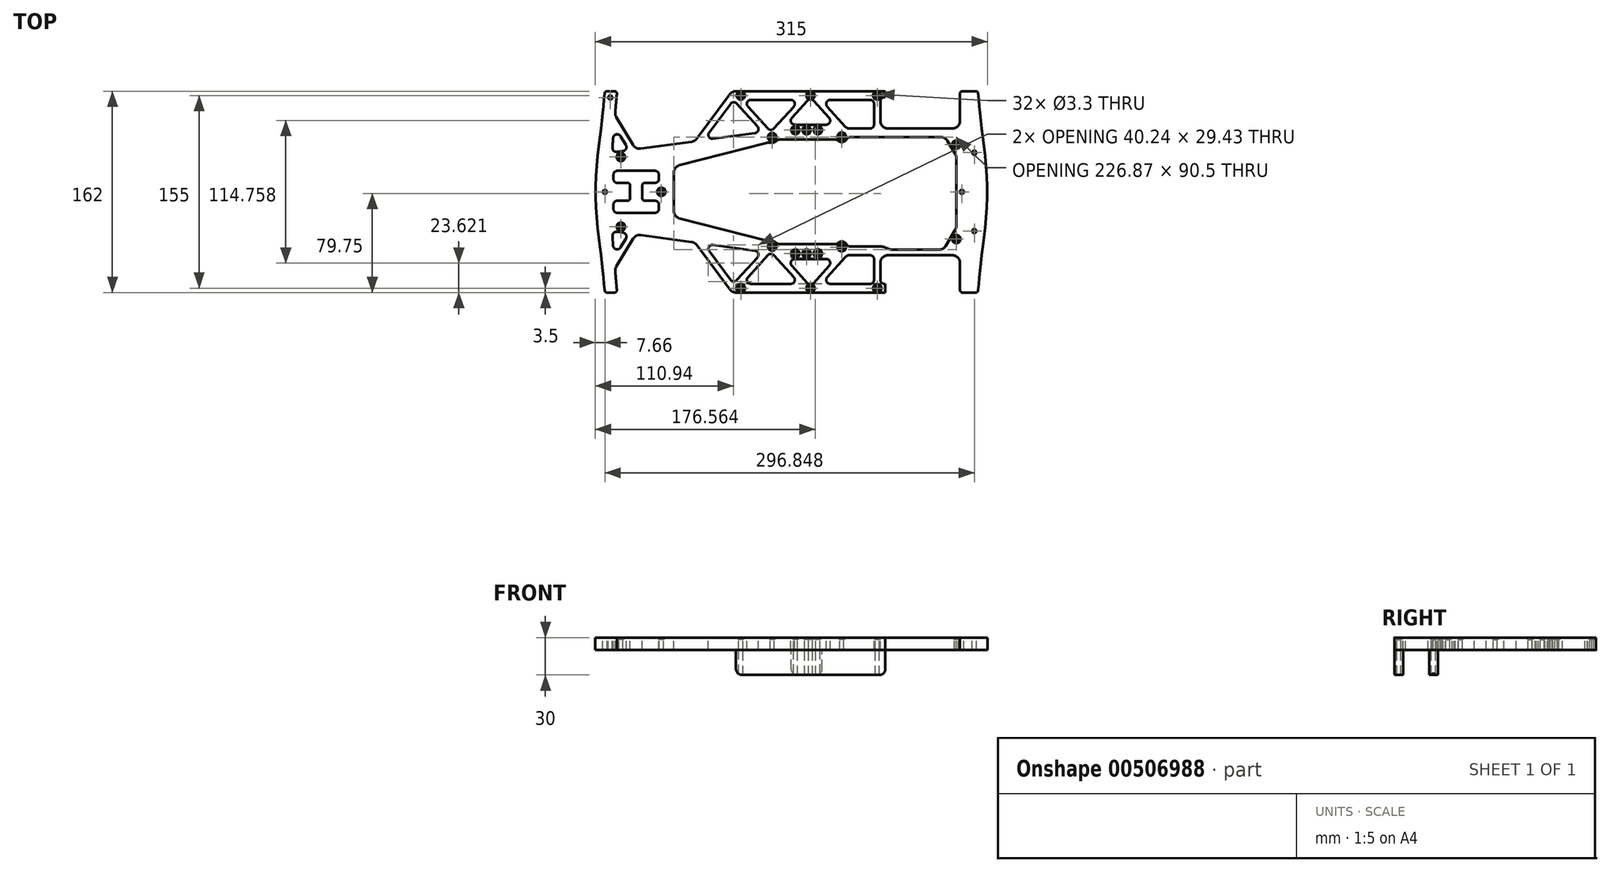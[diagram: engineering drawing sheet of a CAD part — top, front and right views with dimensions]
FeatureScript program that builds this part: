
annotation { "Feature Type Name" : "Feature", "Feature Type Description" : "" }
export const myFeature = defineFeature(function(context is Context, id is Id, definition is map)
    precondition{}
    {
        {
            var Q0;
            Q0=qCreatedBy(makeId("Top.planeOp"),FACE);
            var sketch = newSketch(context, id + "F0", { "sketchPlane" : qUnion([Q0])});
            skLineSegment(sketch, "E0", {"start": v(-44.5, 81) * mm, "end": v(75.5, 81) * mm});
            skLineSegment(sketch, "E1", {"start": v(30.36, 59.43) * mm, "end": v(17.78, 73.34) * mm});
            skLineSegment(sketch, "E2", {"start": v(0.38, 59.43) * mm, "end": v(12.96, 73.34) * mm});
            skLineSegment(sketch, "E3", {"start": v(14.9, 74) * mm, "end": v(15.85, 74) * mm});
            skLineSegment(sketch, "E4", {"start": v(31.25, 74) * mm, "end": v(63.25, 74) * mm});
            skLineSegment(sketch, "E5", {"start": v(-32.5, 74) * mm, "end": v(-0.5, 74) * mm});
            skLineSegment(sketch, "E6", {"start": v(74.75, -74) * mm, "end": v(75.5, -74) * mm});
            skLineSegment(sketch, "E7", {"start": v(31.25, -74) * mm, "end": v(63.25, -74) * mm});
            skLineSegment(sketch, "E8", {"start": v(-32.5, -74) * mm, "end": v(-0.5, -74) * mm});
            skArc(sketch, "E9", {"start": v(131.64, -30.72) * mm, "mid": v(132.28, -29.23) * mm, "end": v(132.5, -27.62) * mm});
            skArc(sketch, "E10", {"start": v(118.73, -46.5) * mm, "mid": v(121.68, -45.72) * mm, "end": v(123.87, -43.6) * mm});
            skArc(sketch, "E11", {"start": v(132.5, 27.62) * mm, "mid": v(132.28, 29.23) * mm, "end": v(131.64, 30.72) * mm});
            skArc(sketch, "E12", {"start": v(125.37, 41.1) * mm, "mid": v(123.19, 43.22) * mm, "end": v(120.24, 44) * mm});
            skLineSegment(sketch, "E13", {"start": v(131.64, 30.72) * mm, "end": v(125.37, 41.1) * mm});
            skArc(sketch, "E14", {"start": v(-89.87, 21.37) * mm, "mid": v(-93.11, 19.23) * mm, "end": v(-94.37, 15.56) * mm});
            skArc(sketch, "E15", {"start": v(-94.37, -15.56) * mm, "mid": v(-93.11, -19.23) * mm, "end": v(-89.87, -21.37) * mm});
            skLineSegment(sketch, "E16", {"start": v(-94.37, -15.56) * mm, "end": v(-94.37, 15.56) * mm});
            skLineSegment(sketch, "E17", {"start": v(131.64, -30.72) * mm, "end": v(123.87, -43.6) * mm});
            skLineSegment(sketch, "E18", {"start": v(-139.75, 16.9) * mm, "end": v(-109.62, 16.9) * mm});
            skLineSegment(sketch, "E19", {"start": v(-139.75, 7.13) * mm, "end": v(-129.57, 7.13) * mm});
            skLineSegment(sketch, "E20", {"start": v(-129.57, -7.13) * mm, "end": v(-129.57, 7.13) * mm});
            skLineSegment(sketch, "E21", {"start": v(-139.75, -7.13) * mm, "end": v(-129.57, -7.13) * mm});
            skLineSegment(sketch, "E22", {"start": v(-139.75, -16.9) * mm, "end": v(-109.62, -16.9) * mm});
            skLineSegment(sketch, "E23", {"start": v(-143, -13.64) * mm, "end": v(-143, -10.38) * mm});
            skLineSegment(sketch, "E24", {"start": v(-143, 10.38) * mm, "end": v(-143, 13.64) * mm});
            skLineSegment(sketch, "E25", {"start": v(-106.37, 13.64) * mm, "end": v(-106.37, 10.38) * mm});
            skLineSegment(sketch, "E26", {"start": v(-106.37, -10.38) * mm, "end": v(-106.37, -13.64) * mm});
            skLineSegment(sketch, "E27", {"start": v(-119.8, -7.13) * mm, "end": v(-109.62, -7.13) * mm});
            skLineSegment(sketch, "E28", {"start": v(-119.8, 7.13) * mm, "end": v(-109.62, 7.13) * mm});
            skLineSegment(sketch, "E29", {"start": v(-119.8, -7.13) * mm, "end": v(-119.8, 7.13) * mm});
            skArc(sketch, "E30", {"start": v(-12.16, -40.95) * mm, "mid": v(-13.66, -39.88) * mm, "end": v(-15.47, -39.5) * mm});
            skArc(sketch, "E31", {"start": v(-15.47, 39.5) * mm, "mid": v(-13.66, 39.88) * mm, "end": v(-12.16, 40.95) * mm});
            skLineSegment(sketch, "E32", {"start": v(2.79, -54) * mm, "end": v(27.95, -54) * mm});
            skLineSegment(sketch, "E33", {"start": v(0.38, -59.43) * mm, "end": v(12.96, -73.34) * mm});
            skLineSegment(sketch, "E34", {"start": v(30.36, -59.43) * mm, "end": v(17.78, -73.34) * mm});
            skLineSegment(sketch, "E35", {"start": v(2.79, 54) * mm, "end": v(27.95, 54) * mm});
            skLineSegment(sketch, "E36", {"start": v(-121.14, 34.71) * mm, "end": v(-80.12, 40.32) * mm});
            skLineSegment(sketch, "E37", {"start": v(-76.13, 42.67) * mm, "end": v(-49.3, 78.59) * mm});
            skArc(sketch, "E38", {"start": v(-18.67, 39.5) * mm, "mid": v(-19.42, 39.45) * mm, "end": v(-20.17, 39.31) * mm});
            skArc(sketch, "E39", {"start": v(79.02, -46.15) * mm, "mid": v(80.02, -46.41) * mm, "end": v(81.04, -46.5) * mm});
            skArc(sketch, "E40", {"start": v(73.98, -44.35) * mm, "mid": v(72.98, -44.09) * mm, "end": v(71.96, -44) * mm});
            skLineSegment(sketch, "E41", {"start": v(81.04, -46.5) * mm, "end": v(82.68, -46.5) * mm});
            skLineSegment(sketch, "E42", {"start": v(73.98, -44.35) * mm, "end": v(79.02, -46.15) * mm});
            skLineSegment(sketch, "E43", {"start": v(81.04, -46.5) * mm, "end": v(118.73, -46.5) * mm});
            skLineSegment(sketch, "E44", {"start": v(77.5, 51) * mm, "end": v(129.5, 51) * mm});
            skArc(sketch, "E45", {"start": v(135.5, -57) * mm, "mid": v(133.74, -52.76) * mm, "end": v(129.5, -51) * mm});
            skLineSegment(sketch, "E46", {"start": v(135.5, -81) * mm, "end": v(135.5, -57) * mm});
            skArc(sketch, "E47", {"start": v(129.5, 51) * mm, "mid": v(133.74, 52.76) * mm, "end": v(135.5, 57) * mm});
            skLineSegment(sketch, "E48", {"start": v(135.5, 81) * mm, "end": v(135.5, 57) * mm});
            skLineSegment(sketch, "E49", {"start": v(132.5, 0) * mm, "end": v(132.5, 27.62) * mm});
            skLineSegment(sketch, "E50", {"start": v(150, 81) * mm, "end": v(135.5, 81) * mm});
            skArc(sketch, "E51", {"start": v(37.48, 41.16) * mm, "mid": v(41.24, 40.06) * mm, "end": v(44.44, 42.32) * mm});
            skLineSegment(sketch, "E52", {"start": v(47.28, 44) * mm, "end": v(120.24, 44) * mm});
            skLineSegment(sketch, "E53", {"start": v(46.18, 51) * mm, "end": v(63.25, 51) * mm});
            skArc(sketch, "E54", {"start": v(71.5, 57) * mm, "mid": v(73.26, 52.76) * mm, "end": v(77.5, 51) * mm});
            skLineSegment(sketch, "E55", {"start": v(71.5, 57) * mm, "end": v(71.5, 72.75) * mm});
            skLineSegment(sketch, "E56", {"start": v(66.5, 54.25) * mm, "end": v(66.5, 70.75) * mm});
            skLineSegment(sketch, "E57", {"start": v(75.5, 76) * mm, "end": v(75.5, 81) * mm});
            skLineSegment(sketch, "E58", {"start": v(74.75, 76) * mm, "end": v(75.5, 76) * mm});
            skLineSegment(sketch, "E59", {"start": v(43.77, 52.07) * mm, "end": v(28.84, 68.57) * mm});
            skLineSegment(sketch, "E60", {"start": v(-9.77, 42) * mm, "end": v(35.3, 42) * mm});
            skLineSegment(sketch, "E61", {"start": v(-18.67, 39.5) * mm, "end": v(-15.47, 39.5) * mm});
            skLineSegment(sketch, "E62", {"start": v(-63, 42.66) * mm, "end": v(-29.24, 47.28) * mm});
            skLineSegment(sketch, "E63", {"start": v(-27.27, 52.68) * mm, "end": v(-43.87, 71.03) * mm});
            skLineSegment(sketch, "E64", {"start": v(-18.9, 50.89) * mm, "end": v(-34.9, 68.57) * mm});
            skLineSegment(sketch, "E65", {"start": v(-14.1, 50.89) * mm, "end": v(1.9, 68.57) * mm});
            skArc(sketch, "E66", {"start": v(-44.5, 81) * mm, "mid": v(-47.19, 80.36) * mm, "end": v(-49.3, 78.59) * mm});
            skArc(sketch, "E67", {"start": v(-80.12, 40.32) * mm, "mid": v(-77.89, 41.1) * mm, "end": v(-76.13, 42.67) * mm});
            skLineSegment(sketch, "E68", {"start": v(-66.04, 47.83) * mm, "end": v(-48.89, 70.8) * mm});
            skLineSegment(sketch, "E69", {"start": v(-20.17, 39.31) * mm, "end": v(-89.87, 21.37) * mm});
            skArc(sketch, "E70", {"start": v(-127.1, 37.56) * mm, "mid": v(-124.54, 35.24) * mm, "end": v(-121.14, 34.71) * mm});
            skLineSegment(sketch, "E71", {"start": v(-140.08, 32.12) * mm, "end": v(-135.33, 32.77) * mm});
            skLineSegment(sketch, "E72", {"start": v(-132.99, 37.66) * mm, "end": v(-137.22, 44.7) * mm});
            skFitSpline(sketch, "E73", {"points": [v(-143.24, 43.25) * mm, v(-143.43, 40.68) * mm, v(-143.6, 38.12) * mm, v(-143.77, 35.55) * mm]});
            skLineSegment(sketch, "E74", {"start": v(-150, 81) * mm, "end": v(-140, 81) * mm});
            skFitSpline(sketch, "E75", {"points": [v(-140, 81) * mm, v(-140.53, 75.29) * mm, v(-141.06, 69.57) * mm, v(-141.56, 63.86) * mm]});
            skLineSegment(sketch, "E76", {"start": v(-127.1, 37.56) * mm, "end": v(-140.73, 60.24) * mm});
            skArc(sketch, "E77", {"start": v(-141.56, 63.86) * mm, "mid": v(-141.43, 61.98) * mm, "end": v(-140.73, 60.24) * mm});
            skLineSegment(sketch, "E78", {"start": v(43.77, -52.07) * mm, "end": v(28.84, -68.57) * mm});
            skArc(sketch, "E79", {"start": v(77.5, -51) * mm, "mid": v(73.26, -52.76) * mm, "end": v(71.5, -57) * mm});
            skLineSegment(sketch, "E80", {"start": v(47.28, -44) * mm, "end": v(71.96, -44) * mm});
            skArc(sketch, "E81", {"start": v(-140.73, -60.24) * mm, "mid": v(-141.43, -61.98) * mm, "end": v(-141.56, -63.86) * mm});
            skArc(sketch, "E82", {"start": v(-121.14, -34.71) * mm, "mid": v(-124.54, -35.24) * mm, "end": v(-127.1, -37.56) * mm});
            skArc(sketch, "E83", {"start": v(-76.13, -42.67) * mm, "mid": v(-77.89, -41.1) * mm, "end": v(-80.12, -40.32) * mm});
            skArc(sketch, "E84", {"start": v(-49.3, -78.59) * mm, "mid": v(-47.19, -80.36) * mm, "end": v(-44.5, -81) * mm});
            skArc(sketch, "E85", {"start": v(-20.17, -39.31) * mm, "mid": v(-19.42, -39.45) * mm, "end": v(-18.67, -39.5) * mm});
            skFitSpline(sketch, "E86", {"points": [v(-143.24, -43.25) * mm, v(-143.43, -40.68) * mm, v(-143.6, -38.12) * mm, v(-143.77, -35.55) * mm]});
            skLineSegment(sketch, "E87", {"start": v(-121.14, -34.71) * mm, "end": v(-80.12, -40.32) * mm});
            skLineSegment(sketch, "E88", {"start": v(-140.08, -32.12) * mm, "end": v(-135.33, -32.77) * mm});
            skLineSegment(sketch, "E89", {"start": v(-127.1, -37.56) * mm, "end": v(-140.73, -60.24) * mm});
            skLineSegment(sketch, "E90", {"start": v(-132.99, -37.66) * mm, "end": v(-137.22, -44.7) * mm});
            skLineSegment(sketch, "E91", {"start": v(-63, -42.66) * mm, "end": v(-29.24, -47.28) * mm});
            skLineSegment(sketch, "E92", {"start": v(77.5, -51) * mm, "end": v(129.5, -51) * mm});
            skLineSegment(sketch, "E93", {"start": v(-150, -81) * mm, "end": v(-140, -81) * mm});
            skLineSegment(sketch, "E94", {"start": v(-14.1, -50.89) * mm, "end": v(1.9, -68.57) * mm});
            skLineSegment(sketch, "E95", {"start": v(-18.9, -50.89) * mm, "end": v(-34.9, -68.57) * mm});
            skLineSegment(sketch, "E96", {"start": v(-27.27, -52.68) * mm, "end": v(-43.87, -71.03) * mm});
            skLineSegment(sketch, "E97", {"start": v(132.5, 0) * mm, "end": v(132.5, -27.62) * mm});
            skFitSpline(sketch, "E98", {"points": [v(-150, -81) * mm, v(-152.5, -54) * mm, v(-157.5, 0) * mm, v(-152.5, 54) * mm, v(-150, 81) * mm]});
            skFitSpline(sketch, "E99", {"points": [v(150, 81) * mm, v(152.5, 54) * mm, v(157.5, 0) * mm, v(152.5, -54) * mm, v(150, -81) * mm]});
            skLineSegment(sketch, "E100", {"start": v(-76.13, -42.67) * mm, "end": v(-49.3, -78.59) * mm});
            skLineSegment(sketch, "E101", {"start": v(75.5, -74) * mm, "end": v(75.5, -81) * mm});
            skLineSegment(sketch, "E102", {"start": v(150, -81) * mm, "end": v(135.5, -81) * mm});
            skLineSegment(sketch, "E103", {"start": v(-44.5, -81) * mm, "end": v(75.5, -81) * mm});
            skLineSegment(sketch, "E104", {"start": v(-66.04, -47.83) * mm, "end": v(-48.89, -70.8) * mm});
            skFitSpline(sketch, "E105", {"points": [v(-140, -81) * mm, v(-140.53, -75.29) * mm, v(-141.06, -69.57) * mm, v(-141.56, -63.86) * mm]});
            skLineSegment(sketch, "E106", {"start": v(66.5, -54.25) * mm, "end": v(66.5, -70.75) * mm});
            skLineSegment(sketch, "E107", {"start": v(71.5, -57) * mm, "end": v(71.5, -70.75) * mm});
            skLineSegment(sketch, "E108", {"start": v(46.18, -51) * mm, "end": v(63.25, -51) * mm});
            skArc(sketch, "E109", {"start": v(44.44, -42.32) * mm, "mid": v(41.24, -40.06) * mm, "end": v(37.48, -41.16) * mm});
            skLineSegment(sketch, "E110", {"start": v(-18.67, -39.5) * mm, "end": v(-15.47, -39.5) * mm});
            skLineSegment(sketch, "E111", {"start": v(-9.77, -42) * mm, "end": v(35.3, -42) * mm});
            skLineSegment(sketch, "E112", {"start": v(-20.17, -39.31) * mm, "end": v(-89.87, -21.37) * mm});
            skArc(sketch, "E113", {"start": v(-137.22, 44.7) * mm, "mid": v(-140.76, 46.18) * mm, "end": v(-143.24, 43.25) * mm});
            skArc(sketch, "E114", {"start": v(-135.33, 32.77) * mm, "mid": v(-132.84, 34.59) * mm, "end": v(-132.99, 37.66) * mm});
            skArc(sketch, "E115", {"start": v(-143.77, 35.55) * mm, "mid": v(-142.74, 32.96) * mm, "end": v(-140.08, 32.12) * mm});
            skArc(sketch, "E116", {"start": v(-139.75, 16.9) * mm, "mid": v(-142.05, 15.94) * mm, "end": v(-143, 13.64) * mm});
            skArc(sketch, "E117", {"start": v(-143, 10.38) * mm, "mid": v(-142.05, 8.08) * mm, "end": v(-139.75, 7.13) * mm});
            skArc(sketch, "E118", {"start": v(-106.37, 13.64) * mm, "mid": v(-107.32, 15.94) * mm, "end": v(-109.62, 16.9) * mm});
            skArc(sketch, "E119", {"start": v(-109.62, 7.13) * mm, "mid": v(-107.32, 8.08) * mm, "end": v(-106.37, 10.38) * mm});
            skArc(sketch, "E120", {"start": v(-106.37, -10.38) * mm, "mid": v(-107.32, -8.08) * mm, "end": v(-109.62, -7.13) * mm});
            skArc(sketch, "E121", {"start": v(-109.62, -16.9) * mm, "mid": v(-107.32, -15.94) * mm, "end": v(-106.37, -13.64) * mm});
            skArc(sketch, "E122", {"start": v(-139.75, -7.13) * mm, "mid": v(-142.05, -8.08) * mm, "end": v(-143, -10.38) * mm});
            skArc(sketch, "E123", {"start": v(-143, -13.64) * mm, "mid": v(-142.05, -15.94) * mm, "end": v(-139.75, -16.9) * mm});
            skArc(sketch, "E124", {"start": v(-140.08, -32.12) * mm, "mid": v(-142.74, -32.96) * mm, "end": v(-143.77, -35.55) * mm});
            skArc(sketch, "E125", {"start": v(-143.24, -43.25) * mm, "mid": v(-140.76, -46.18) * mm, "end": v(-137.22, -44.7) * mm});
            skArc(sketch, "E126", {"start": v(-132.99, -37.66) * mm, "mid": v(-132.84, -34.59) * mm, "end": v(-135.33, -32.77) * mm});
            skArc(sketch, "E127", {"start": v(-63, -42.66) * mm, "mid": v(-66.23, -44.23) * mm, "end": v(-66.04, -47.83) * mm});
            skArc(sketch, "E128", {"start": v(-27.27, -52.68) * mm, "mid": v(-26.63, -49.38) * mm, "end": v(-29.24, -47.28) * mm});
            skArc(sketch, "E129", {"start": v(-48.89, -70.8) * mm, "mid": v(-46.44, -72.1) * mm, "end": v(-43.87, -71.03) * mm});
            skArc(sketch, "E130", {"start": v(-14.1, -50.89) * mm, "mid": v(-16.5, -49.82) * mm, "end": v(-18.9, -50.89) * mm});
            skArc(sketch, "E131", {"start": v(-34.9, -68.57) * mm, "mid": v(-35.47, -72.07) * mm, "end": v(-32.5, -74) * mm});
            skArc(sketch, "E132", {"start": v(-0.5, -74) * mm, "mid": v(2.47, -72.07) * mm, "end": v(1.9, -68.57) * mm});
            skArc(sketch, "E133", {"start": v(2.79, -54) * mm, "mid": v(-0.18, -55.93) * mm, "end": v(0.38, -59.43) * mm});
            skArc(sketch, "E134", {"start": v(12.96, -73.34) * mm, "mid": v(15.37, -74.4) * mm, "end": v(17.78, -73.34) * mm});
            skArc(sketch, "E135", {"start": v(30.36, -59.43) * mm, "mid": v(30.92, -55.93) * mm, "end": v(27.95, -54) * mm});
            skArc(sketch, "E136", {"start": v(28.84, -68.57) * mm, "mid": v(28.28, -72.07) * mm, "end": v(31.25, -74) * mm});
            skArc(sketch, "E137", {"start": v(46.18, -51) * mm, "mid": v(44.86, -51.28) * mm, "end": v(43.77, -52.07) * mm});
            skArc(sketch, "E138", {"start": v(66.5, -54.25) * mm, "mid": v(65.55, -51.95) * mm, "end": v(63.25, -51) * mm});
            skArc(sketch, "E139", {"start": v(63.25, -74) * mm, "mid": v(65.55, -73.05) * mm, "end": v(66.5, -70.75) * mm});
            skArc(sketch, "E140", {"start": v(71.5, -70.75) * mm, "mid": v(72.45, -73.05) * mm, "end": v(74.75, -74) * mm});
            skArc(sketch, "E141", {"start": v(-12.16, -40.95) * mm, "mid": v(-11.07, -41.73) * mm, "end": v(-9.77, -42) * mm});
            skArc(sketch, "E142", {"start": v(35.3, -42) * mm, "mid": v(36.47, -41.78) * mm, "end": v(37.48, -41.16) * mm});
            skArc(sketch, "E143", {"start": v(44.44, -42.32) * mm, "mid": v(45.63, -43.55) * mm, "end": v(47.28, -44) * mm});
            skArc(sketch, "E144", {"start": v(-9.77, 42) * mm, "mid": v(-11.07, 41.73) * mm, "end": v(-12.16, 40.95) * mm});
            skArc(sketch, "E145", {"start": v(37.48, 41.16) * mm, "mid": v(36.47, 41.78) * mm, "end": v(35.3, 42) * mm});
            skArc(sketch, "E146", {"start": v(47.28, 44) * mm, "mid": v(45.63, 43.55) * mm, "end": v(44.44, 42.32) * mm});
            skArc(sketch, "E147", {"start": v(-66.04, 47.83) * mm, "mid": v(-66.23, 44.23) * mm, "end": v(-63, 42.66) * mm});
            skArc(sketch, "E148", {"start": v(-43.87, 71.03) * mm, "mid": v(-46.44, 72.1) * mm, "end": v(-48.89, 70.8) * mm});
            skArc(sketch, "E149", {"start": v(-29.24, 47.28) * mm, "mid": v(-26.63, 49.38) * mm, "end": v(-27.27, 52.68) * mm});
            skArc(sketch, "E150", {"start": v(-18.9, 50.89) * mm, "mid": v(-16.5, 49.82) * mm, "end": v(-14.1, 50.89) * mm});
            skArc(sketch, "E151", {"start": v(-32.5, 74) * mm, "mid": v(-35.47, 72.07) * mm, "end": v(-34.9, 68.57) * mm});
            skArc(sketch, "E152", {"start": v(1.9, 68.57) * mm, "mid": v(2.47, 72.07) * mm, "end": v(-0.5, 74) * mm});
            skArc(sketch, "E153", {"start": v(17.78, 73.34) * mm, "mid": v(15.37, 74.4) * mm, "end": v(12.96, 73.34) * mm});
            skArc(sketch, "E154", {"start": v(0.38, 59.43) * mm, "mid": v(-0.18, 55.93) * mm, "end": v(2.79, 54) * mm});
            skArc(sketch, "E155", {"start": v(27.95, 54) * mm, "mid": v(30.92, 55.93) * mm, "end": v(30.36, 59.43) * mm});
            skArc(sketch, "E156", {"start": v(43.77, 52.07) * mm, "mid": v(44.86, 51.28) * mm, "end": v(46.18, 51) * mm});
            skArc(sketch, "E157", {"start": v(31.25, 74) * mm, "mid": v(28.28, 72.07) * mm, "end": v(28.84, 68.57) * mm});
            skArc(sketch, "E158", {"start": v(66.5, 70.75) * mm, "mid": v(65.55, 73.05) * mm, "end": v(63.25, 74) * mm});
            skArc(sketch, "E159", {"start": v(63.25, 51) * mm, "mid": v(65.55, 51.95) * mm, "end": v(66.5, 54.25) * mm});
            skArc(sketch, "E160", {"start": v(74.75, 76) * mm, "mid": v(72.45, 75.05) * mm, "end": v(71.5, 72.75) * mm});
            skPoint(sketch, "E161", {"position": v(-137, 28) * mm});
            skPoint(sketch, "E162", {"position": v(-104.5, 0) * mm});
            skPoint(sketch, "E163", {"position": v(-149.84, 0) * mm});
            skPoint(sketch, "E164", {"position": v(-137, -28) * mm});
            skPoint(sketch, "E165", {"position": v(-70.5, -31) * mm});
            skPoint(sketch, "E166", {"position": v(-70.5, 31) * mm});
            skPoint(sketch, "E167", {"position": v(3.25, 49.62) * mm});
            skPoint(sketch, "E168", {"position": v(12.25, 49.62) * mm});
            skPoint(sketch, "E169", {"position": v(21.25, 49.62) * mm});
            skPoint(sketch, "E170", {"position": v(15.37, 77.5) * mm});
            skPoint(sketch, "E171", {"position": v(-40.63, 77.5) * mm});
            skPoint(sketch, "E172", {"position": v(69, 77.5) * mm});
            skPoint(sketch, "E173", {"position": v(-145.48, 75.87) * mm});
            skPoint(sketch, "E174", {"position": v(-40.63, -77.5) * mm});
            skPoint(sketch, "E175", {"position": v(3.25, -49.62) * mm});
            skPoint(sketch, "E176", {"position": v(12.25, -49.62) * mm});
            skPoint(sketch, "E177", {"position": v(21.25, -49.62) * mm});
            skPoint(sketch, "E178", {"position": v(15.37, -77.5) * mm});
            skPoint(sketch, "E179", {"position": v(69, -77.5) * mm});
            skPoint(sketch, "E180", {"position": v(132.5, -38) * mm});
            skPoint(sketch, "E181", {"position": v(147, -31.5) * mm});
            skPoint(sketch, "E182", {"position": v(137, 0) * mm});
            skPoint(sketch, "E183", {"position": v(147, 31.5) * mm});
            skPoint(sketch, "E184", {"position": v(132.5, 38) * mm});
            skSolve(sketch);
        }
        {
            var Q0;
            Q0=makeQuery(id+"F0.imprint","IMPRINT",FACE,{"disambiguationData":[TD([[makeQuery(id+"F0.imprint","IMPRINT",EDGE,{"derivedFrom":sQuery(id+"F0.wireOp",EDGE,"E0")}),-1.0]])]});
            extrude(context, id + "F1", {"entities" : qUnion([Q0]), "oppositeDirection" : true, "depth" : 10 * mm, "offsetDistance" : 25 * mm});
        }
        {
            var Q0;
            Q0=makeQuery(id+"F1.opExtrude","SWEPT_EDGE",EDGE,{"disambiguationData":[OSD([sQuery(id+"F0.wireOp",EDGE,"E93"),sQuery(id+"F0.wireOp",EDGE,"E98")])]});
            var Q1;
            Q1=makeQuery(id+"F1.opExtrude","SWEPT_EDGE",EDGE,{"disambiguationData":[OSD([sQuery(id+"F0.wireOp",EDGE,"E93"),sQuery(id+"F0.wireOp",EDGE,"E105")])]});
            var Q2;
            Q2=makeQuery(id+"F1.opExtrude","SWEPT_EDGE",EDGE,{"disambiguationData":[OSD([sQuery(id+"F0.wireOp",EDGE,"E74"),sQuery(id+"F0.wireOp",EDGE,"E98")])]});
            var Q3;
            Q3=makeQuery(id+"F1.opExtrude","SWEPT_EDGE",EDGE,{"disambiguationData":[OSD([sQuery(id+"F0.wireOp",EDGE,"E74"),sQuery(id+"F0.wireOp",EDGE,"E75")])]});
            var Q4;
            Q4=makeQuery(id+"F1.opExtrude","SWEPT_EDGE",EDGE,{"disambiguationData":[OSD([sQuery(id+"F0.wireOp",EDGE,"E50"),sQuery(id+"F0.wireOp",EDGE,"E99")])]});
            var Q5;
            Q5=makeQuery(id+"F1.opExtrude","SWEPT_EDGE",EDGE,{"disambiguationData":[OSD([sQuery(id+"F0.wireOp",EDGE,"E48"),sQuery(id+"F0.wireOp",EDGE,"E50")])]});
            var Q6;
            Q6=makeQuery(id+"F1.opExtrude","SWEPT_EDGE",EDGE,{"disambiguationData":[OSD([sQuery(id+"F0.wireOp",EDGE,"E99"),sQuery(id+"F0.wireOp",EDGE,"E102")])]});
            var Q7;
            Q7=makeQuery(id+"F1.opExtrude","SWEPT_EDGE",EDGE,{"disambiguationData":[OSD([sQuery(id+"F0.wireOp",EDGE,"E46"),sQuery(id+"F0.wireOp",EDGE,"E102")])]});
            var Q8;
            Q8=makeQuery(id+"F1.opExtrude","SWEPT_EDGE",EDGE,{"disambiguationData":[OSD([sQuery(id+"F0.wireOp",EDGE,"E27"),sQuery(id+"F0.wireOp",EDGE,"E29")])]});
            var Q9;
            Q9=makeQuery(id+"F1.opExtrude","SWEPT_EDGE",EDGE,{"disambiguationData":[OSD([sQuery(id+"F0.wireOp",EDGE,"E20"),sQuery(id+"F0.wireOp",EDGE,"E21")])]});
            var Q10;
            Q10=makeQuery(id+"F1.opExtrude","SWEPT_EDGE",EDGE,{"disambiguationData":[OSD([sQuery(id+"F0.wireOp",EDGE,"E28"),sQuery(id+"F0.wireOp",EDGE,"E29")])]});
            var Q11;
            Q11=makeQuery(id+"F1.opExtrude","SWEPT_EDGE",EDGE,{"disambiguationData":[OSD([sQuery(id+"F0.wireOp",EDGE,"E19"),sQuery(id+"F0.wireOp",EDGE,"E20")])]});
            fillet(context, id + "F2", {"entities" : qUnion([Q0, Q1, Q2, Q3, Q4, Q5, Q6, Q7, Q8, Q9, Q10, Q11]), "radius" : 2 * mm, "tangentPropagation" : true, "allowEdgeOverflow" : false});
        }
        {
            var Q0;
            Q0=sQuery(id+"F0.wireOp",VERTEX,"E173");
            var Q1;
            Q1=sQuery(id+"F0.wireOp",VERTEX,"E163");
            var Q2;
            Q2=sQuery(id+"F0.wireOp",VERTEX,"E183");
            var Q3;
            Q3=sQuery(id+"F0.wireOp",VERTEX,"E181");
            var Q4;
            Q4=sQuery(id+"F0.wireOp",VERTEX,"E182");
            var Q5;
            Q5=makeQuery(id+"F1.opExtrude","SWEPT_BODY",BODY,{"disambiguationData":[OSD([sQuery(id+"F0.wireOp",EDGE,"E0"),sQuery(id+"F0.wireOp",EDGE,"E1"),sQuery(id+"F0.wireOp",EDGE,"E2"),sQuery(id+"F0.wireOp",EDGE,"E4"),sQuery(id+"F0.wireOp",EDGE,"E5"),sQuery(id+"F0.wireOp",EDGE,"E6"),sQuery(id+"F0.wireOp",EDGE,"E7"),sQuery(id+"F0.wireOp",EDGE,"E8"),sQuery(id+"F0.wireOp",EDGE,"E9"),sQuery(id+"F0.wireOp",EDGE,"E10"),sQuery(id+"F0.wireOp",EDGE,"E11"),sQuery(id+"F0.wireOp",EDGE,"E12"),sQuery(id+"F0.wireOp",EDGE,"E13"),sQuery(id+"F0.wireOp",EDGE,"E14"),sQuery(id+"F0.wireOp",EDGE,"E15"),sQuery(id+"F0.wireOp",EDGE,"E16"),sQuery(id+"F0.wireOp",EDGE,"E17"),sQuery(id+"F0.wireOp",EDGE,"E18"),sQuery(id+"F0.wireOp",EDGE,"E19"),sQuery(id+"F0.wireOp",EDGE,"E20"),sQuery(id+"F0.wireOp",EDGE,"E21"),sQuery(id+"F0.wireOp",EDGE,"E22"),sQuery(id+"F0.wireOp",EDGE,"E23"),sQuery(id+"F0.wireOp",EDGE,"E24"),sQuery(id+"F0.wireOp",EDGE,"E25"),sQuery(id+"F0.wireOp",EDGE,"E26"),sQuery(id+"F0.wireOp",EDGE,"E27"),sQuery(id+"F0.wireOp",EDGE,"E28"),sQuery(id+"F0.wireOp",EDGE,"E29"),sQuery(id+"F0.wireOp",EDGE,"E30"),sQuery(id+"F0.wireOp",EDGE,"E31"),sQuery(id+"F0.wireOp",EDGE,"E32"),sQuery(id+"F0.wireOp",EDGE,"E33"),sQuery(id+"F0.wireOp",EDGE,"E34"),sQuery(id+"F0.wireOp",EDGE,"E35"),sQuery(id+"F0.wireOp",EDGE,"E36"),sQuery(id+"F0.wireOp",EDGE,"E37"),sQuery(id+"F0.wireOp",EDGE,"E38"),sQuery(id+"F0.wireOp",EDGE,"E39"),sQuery(id+"F0.wireOp",EDGE,"E40"),sQuery(id+"F0.wireOp",EDGE,"E42"),sQuery(id+"F0.wireOp",EDGE,"E43"),sQuery(id+"F0.wireOp",EDGE,"E45"),sQuery(id+"F0.wireOp",EDGE,"E46"),sQuery(id+"F0.wireOp",EDGE,"E47"),sQuery(id+"F0.wireOp",EDGE,"E48"),sQuery(id+"F0.wireOp",EDGE,"E49"),sQuery(id+"F0.wireOp",EDGE,"E50"),sQuery(id+"F0.wireOp",EDGE,"E44"),sQuery(id+"F0.wireOp",EDGE,"E51"),sQuery(id+"F0.wireOp",EDGE,"E52"),sQuery(id+"F0.wireOp",EDGE,"E53"),sQuery(id+"F0.wireOp",EDGE,"E54"),sQuery(id+"F0.wireOp",EDGE,"E55"),sQuery(id+"F0.wireOp",EDGE,"E56"),sQuery(id+"F0.wireOp",EDGE,"E57"),sQuery(id+"F0.wireOp",EDGE,"E58"),sQuery(id+"F0.wireOp",EDGE,"E59"),sQuery(id+"F0.wireOp",EDGE,"E60"),sQuery(id+"F0.wireOp",EDGE,"E61"),sQuery(id+"F0.wireOp",EDGE,"E62"),sQuery(id+"F0.wireOp",EDGE,"E63"),sQuery(id+"F0.wireOp",EDGE,"E64"),sQuery(id+"F0.wireOp",EDGE,"E65"),sQuery(id+"F0.wireOp",EDGE,"E66"),sQuery(id+"F0.wireOp",EDGE,"E67"),sQuery(id+"F0.wireOp",EDGE,"E68"),sQuery(id+"F0.wireOp",EDGE,"E69"),sQuery(id+"F0.wireOp",EDGE,"E70"),sQuery(id+"F0.wireOp",EDGE,"E71"),sQuery(id+"F0.wireOp",EDGE,"E72"),sQuery(id+"F0.wireOp",EDGE,"E73"),sQuery(id+"F0.wireOp",EDGE,"E74"),sQuery(id+"F0.wireOp",EDGE,"E75"),sQuery(id+"F0.wireOp",EDGE,"E76"),sQuery(id+"F0.wireOp",EDGE,"E77"),sQuery(id+"F0.wireOp",EDGE,"E78"),sQuery(id+"F0.wireOp",EDGE,"E79"),sQuery(id+"F0.wireOp",EDGE,"E80"),sQuery(id+"F0.wireOp",EDGE,"E81"),sQuery(id+"F0.wireOp",EDGE,"E82"),sQuery(id+"F0.wireOp",EDGE,"E83"),sQuery(id+"F0.wireOp",EDGE,"E84"),sQuery(id+"F0.wireOp",EDGE,"E85"),sQuery(id+"F0.wireOp",EDGE,"E86"),sQuery(id+"F0.wireOp",EDGE,"E87"),sQuery(id+"F0.wireOp",EDGE,"E88"),sQuery(id+"F0.wireOp",EDGE,"E89"),sQuery(id+"F0.wireOp",EDGE,"E90"),sQuery(id+"F0.wireOp",EDGE,"E91"),sQuery(id+"F0.wireOp",EDGE,"E92"),sQuery(id+"F0.wireOp",EDGE,"E93"),sQuery(id+"F0.wireOp",EDGE,"E94"),sQuery(id+"F0.wireOp",EDGE,"E95"),sQuery(id+"F0.wireOp",EDGE,"E96"),sQuery(id+"F0.wireOp",EDGE,"E97"),sQuery(id+"F0.wireOp",EDGE,"E98"),sQuery(id+"F0.wireOp",EDGE,"E99"),sQuery(id+"F0.wireOp",EDGE,"E100"),sQuery(id+"F0.wireOp",EDGE,"E101"),sQuery(id+"F0.wireOp",EDGE,"E102"),sQuery(id+"F0.wireOp",EDGE,"E103"),sQuery(id+"F0.wireOp",EDGE,"E104"),sQuery(id+"F0.wireOp",EDGE,"E105"),sQuery(id+"F0.wireOp",EDGE,"E106"),sQuery(id+"F0.wireOp",EDGE,"E107"),sQuery(id+"F0.wireOp",EDGE,"E108"),sQuery(id+"F0.wireOp",EDGE,"E109"),sQuery(id+"F0.wireOp",EDGE,"E110"),sQuery(id+"F0.wireOp",EDGE,"E111"),sQuery(id+"F0.wireOp",EDGE,"E112"),sQuery(id+"F0.wireOp",EDGE,"E113"),sQuery(id+"F0.wireOp",EDGE,"E114"),sQuery(id+"F0.wireOp",EDGE,"E115"),sQuery(id+"F0.wireOp",EDGE,"E116"),sQuery(id+"F0.wireOp",EDGE,"E117"),sQuery(id+"F0.wireOp",EDGE,"E118"),sQuery(id+"F0.wireOp",EDGE,"E119"),sQuery(id+"F0.wireOp",EDGE,"E120"),sQuery(id+"F0.wireOp",EDGE,"E121"),sQuery(id+"F0.wireOp",EDGE,"E122"),sQuery(id+"F0.wireOp",EDGE,"E123"),sQuery(id+"F0.wireOp",EDGE,"E124"),sQuery(id+"F0.wireOp",EDGE,"E125"),sQuery(id+"F0.wireOp",EDGE,"E126"),sQuery(id+"F0.wireOp",EDGE,"E127"),sQuery(id+"F0.wireOp",EDGE,"E128"),sQuery(id+"F0.wireOp",EDGE,"E129"),sQuery(id+"F0.wireOp",EDGE,"E130"),sQuery(id+"F0.wireOp",EDGE,"E131"),sQuery(id+"F0.wireOp",EDGE,"E132"),sQuery(id+"F0.wireOp",EDGE,"E133"),sQuery(id+"F0.wireOp",EDGE,"E134"),sQuery(id+"F0.wireOp",EDGE,"E135"),sQuery(id+"F0.wireOp",EDGE,"E136"),sQuery(id+"F0.wireOp",EDGE,"E137"),sQuery(id+"F0.wireOp",EDGE,"E138"),sQuery(id+"F0.wireOp",EDGE,"E139"),sQuery(id+"F0.wireOp",EDGE,"E140"),sQuery(id+"F0.wireOp",EDGE,"E141"),sQuery(id+"F0.wireOp",EDGE,"E142"),sQuery(id+"F0.wireOp",EDGE,"E143"),sQuery(id+"F0.wireOp",EDGE,"E144"),sQuery(id+"F0.wireOp",EDGE,"E145"),sQuery(id+"F0.wireOp",EDGE,"E146"),sQuery(id+"F0.wireOp",EDGE,"E147"),sQuery(id+"F0.wireOp",EDGE,"E148"),sQuery(id+"F0.wireOp",EDGE,"E149"),sQuery(id+"F0.wireOp",EDGE,"E150"),sQuery(id+"F0.wireOp",EDGE,"E151"),sQuery(id+"F0.wireOp",EDGE,"E152"),sQuery(id+"F0.wireOp",EDGE,"E153"),sQuery(id+"F0.wireOp",EDGE,"E154"),sQuery(id+"F0.wireOp",EDGE,"E155"),sQuery(id+"F0.wireOp",EDGE,"E156"),sQuery(id+"F0.wireOp",EDGE,"E157"),sQuery(id+"F0.wireOp",EDGE,"E158"),sQuery(id+"F0.wireOp",EDGE,"E159"),sQuery(id+"F0.wireOp",EDGE,"E160")])]});
            hole(context, id + "F3", {"style" : HoleStyle.SIMPLE, "endStyle" : HoleEndStyle.THROUGH, "standardTappedOrClearance" : lookupTablePath({ "standard" : "ISO", "fit" : "Normal", "size" : "M3", "type" : "Clearance" }), "standardBlindInLast" : lookupTablePath({ "fit" : "Standard", "standard" : "ISO", "size" : "M3", "type" : "Clearance" }), "holeDiameter" : 3.3 * mm, "isTappedThrough" : true, "tappedDepth" : 12 * mm, "tapClearance" : 3, "startFromSketch" : true, "locations" : qUnion([Q0, Q1, Q2, Q3, Q4]), "scope" : qUnion([Q5])});
        }
        {
            var Q0;
            Q0=sQuery(id+"F0.wireOp",VERTEX,"E161");
            var Q1;
            Q1=sQuery(id+"F0.wireOp",VERTEX,"E164");
            var Q2;
            Q2=sQuery(id+"F0.wireOp",VERTEX,"E162");
            var Q3;
            Q3=sQuery(id+"F0.wireOp",VERTEX,"E31.center");
            var Q4;
            Q4=sQuery(id+"F0.wireOp",VERTEX,"E171");
            var Q5;
            Q5=sQuery(id+"F0.wireOp",VERTEX,"E170");
            var Q6;
            Q6=sQuery(id+"F0.wireOp",VERTEX,"E167");
            var Q7;
            Q7=sQuery(id+"F0.wireOp",VERTEX,"E168");
            var Q8;
            Q8=sQuery(id+"F0.wireOp",VERTEX,"E169");
            var Q9;
            Q9=sQuery(id+"F0.wireOp",VERTEX,"E51.center");
            var Q10;
            Q10=sQuery(id+"F0.wireOp",VERTEX,"E172");
            var Q11;
            Q11=sQuery(id+"F0.wireOp",VERTEX,"E184");
            var Q12;
            Q12=sQuery(id+"F0.wireOp",VERTEX,"E180");
            var Q13;
            Q13=sQuery(id+"F0.wireOp",VERTEX,"E109.center");
            var Q14;
            Q14=sQuery(id+"F0.wireOp",VERTEX,"E177");
            var Q15;
            Q15=sQuery(id+"F0.wireOp",VERTEX,"E176");
            var Q16;
            Q16=sQuery(id+"F0.wireOp",VERTEX,"E175");
            var Q17;
            Q17=sQuery(id+"F0.wireOp",VERTEX,"E30.center");
            var Q18;
            Q18=sQuery(id+"F0.wireOp",VERTEX,"E174");
            var Q19;
            Q19=sQuery(id+"F0.wireOp",VERTEX,"E178");
            var Q20;
            Q20=sQuery(id+"F0.wireOp",VERTEX,"E179");
            var Q21;
            Q21=makeQuery(id+"F1.opExtrude","SWEPT_BODY",BODY,{"disambiguationData":[OSD([sQuery(id+"F0.wireOp",EDGE,"E0"),sQuery(id+"F0.wireOp",EDGE,"E1"),sQuery(id+"F0.wireOp",EDGE,"E2"),sQuery(id+"F0.wireOp",EDGE,"E4"),sQuery(id+"F0.wireOp",EDGE,"E5"),sQuery(id+"F0.wireOp",EDGE,"E6"),sQuery(id+"F0.wireOp",EDGE,"E7"),sQuery(id+"F0.wireOp",EDGE,"E8"),sQuery(id+"F0.wireOp",EDGE,"E9"),sQuery(id+"F0.wireOp",EDGE,"E10"),sQuery(id+"F0.wireOp",EDGE,"E11"),sQuery(id+"F0.wireOp",EDGE,"E12"),sQuery(id+"F0.wireOp",EDGE,"E13"),sQuery(id+"F0.wireOp",EDGE,"E14"),sQuery(id+"F0.wireOp",EDGE,"E15"),sQuery(id+"F0.wireOp",EDGE,"E16"),sQuery(id+"F0.wireOp",EDGE,"E17"),sQuery(id+"F0.wireOp",EDGE,"E18"),sQuery(id+"F0.wireOp",EDGE,"E19"),sQuery(id+"F0.wireOp",EDGE,"E20"),sQuery(id+"F0.wireOp",EDGE,"E21"),sQuery(id+"F0.wireOp",EDGE,"E22"),sQuery(id+"F0.wireOp",EDGE,"E23"),sQuery(id+"F0.wireOp",EDGE,"E24"),sQuery(id+"F0.wireOp",EDGE,"E25"),sQuery(id+"F0.wireOp",EDGE,"E26"),sQuery(id+"F0.wireOp",EDGE,"E27"),sQuery(id+"F0.wireOp",EDGE,"E28"),sQuery(id+"F0.wireOp",EDGE,"E29"),sQuery(id+"F0.wireOp",EDGE,"E30"),sQuery(id+"F0.wireOp",EDGE,"E31"),sQuery(id+"F0.wireOp",EDGE,"E32"),sQuery(id+"F0.wireOp",EDGE,"E33"),sQuery(id+"F0.wireOp",EDGE,"E34"),sQuery(id+"F0.wireOp",EDGE,"E35"),sQuery(id+"F0.wireOp",EDGE,"E36"),sQuery(id+"F0.wireOp",EDGE,"E37"),sQuery(id+"F0.wireOp",EDGE,"E38"),sQuery(id+"F0.wireOp",EDGE,"E39"),sQuery(id+"F0.wireOp",EDGE,"E40"),sQuery(id+"F0.wireOp",EDGE,"E42"),sQuery(id+"F0.wireOp",EDGE,"E43"),sQuery(id+"F0.wireOp",EDGE,"E45"),sQuery(id+"F0.wireOp",EDGE,"E46"),sQuery(id+"F0.wireOp",EDGE,"E47"),sQuery(id+"F0.wireOp",EDGE,"E48"),sQuery(id+"F0.wireOp",EDGE,"E49"),sQuery(id+"F0.wireOp",EDGE,"E50"),sQuery(id+"F0.wireOp",EDGE,"E44"),sQuery(id+"F0.wireOp",EDGE,"E51"),sQuery(id+"F0.wireOp",EDGE,"E52"),sQuery(id+"F0.wireOp",EDGE,"E53"),sQuery(id+"F0.wireOp",EDGE,"E54"),sQuery(id+"F0.wireOp",EDGE,"E55"),sQuery(id+"F0.wireOp",EDGE,"E56"),sQuery(id+"F0.wireOp",EDGE,"E57"),sQuery(id+"F0.wireOp",EDGE,"E58"),sQuery(id+"F0.wireOp",EDGE,"E59"),sQuery(id+"F0.wireOp",EDGE,"E60"),sQuery(id+"F0.wireOp",EDGE,"E61"),sQuery(id+"F0.wireOp",EDGE,"E62"),sQuery(id+"F0.wireOp",EDGE,"E63"),sQuery(id+"F0.wireOp",EDGE,"E64"),sQuery(id+"F0.wireOp",EDGE,"E65"),sQuery(id+"F0.wireOp",EDGE,"E66"),sQuery(id+"F0.wireOp",EDGE,"E67"),sQuery(id+"F0.wireOp",EDGE,"E68"),sQuery(id+"F0.wireOp",EDGE,"E69"),sQuery(id+"F0.wireOp",EDGE,"E70"),sQuery(id+"F0.wireOp",EDGE,"E71"),sQuery(id+"F0.wireOp",EDGE,"E72"),sQuery(id+"F0.wireOp",EDGE,"E73"),sQuery(id+"F0.wireOp",EDGE,"E74"),sQuery(id+"F0.wireOp",EDGE,"E75"),sQuery(id+"F0.wireOp",EDGE,"E76"),sQuery(id+"F0.wireOp",EDGE,"E77"),sQuery(id+"F0.wireOp",EDGE,"E78"),sQuery(id+"F0.wireOp",EDGE,"E79"),sQuery(id+"F0.wireOp",EDGE,"E80"),sQuery(id+"F0.wireOp",EDGE,"E81"),sQuery(id+"F0.wireOp",EDGE,"E82"),sQuery(id+"F0.wireOp",EDGE,"E83"),sQuery(id+"F0.wireOp",EDGE,"E84"),sQuery(id+"F0.wireOp",EDGE,"E85"),sQuery(id+"F0.wireOp",EDGE,"E86"),sQuery(id+"F0.wireOp",EDGE,"E87"),sQuery(id+"F0.wireOp",EDGE,"E88"),sQuery(id+"F0.wireOp",EDGE,"E89"),sQuery(id+"F0.wireOp",EDGE,"E90"),sQuery(id+"F0.wireOp",EDGE,"E91"),sQuery(id+"F0.wireOp",EDGE,"E92"),sQuery(id+"F0.wireOp",EDGE,"E93"),sQuery(id+"F0.wireOp",EDGE,"E94"),sQuery(id+"F0.wireOp",EDGE,"E95"),sQuery(id+"F0.wireOp",EDGE,"E96"),sQuery(id+"F0.wireOp",EDGE,"E97"),sQuery(id+"F0.wireOp",EDGE,"E98"),sQuery(id+"F0.wireOp",EDGE,"E99"),sQuery(id+"F0.wireOp",EDGE,"E100"),sQuery(id+"F0.wireOp",EDGE,"E101"),sQuery(id+"F0.wireOp",EDGE,"E102"),sQuery(id+"F0.wireOp",EDGE,"E103"),sQuery(id+"F0.wireOp",EDGE,"E104"),sQuery(id+"F0.wireOp",EDGE,"E105"),sQuery(id+"F0.wireOp",EDGE,"E106"),sQuery(id+"F0.wireOp",EDGE,"E107"),sQuery(id+"F0.wireOp",EDGE,"E108"),sQuery(id+"F0.wireOp",EDGE,"E109"),sQuery(id+"F0.wireOp",EDGE,"E110"),sQuery(id+"F0.wireOp",EDGE,"E111"),sQuery(id+"F0.wireOp",EDGE,"E112"),sQuery(id+"F0.wireOp",EDGE,"E113"),sQuery(id+"F0.wireOp",EDGE,"E114"),sQuery(id+"F0.wireOp",EDGE,"E115"),sQuery(id+"F0.wireOp",EDGE,"E116"),sQuery(id+"F0.wireOp",EDGE,"E117"),sQuery(id+"F0.wireOp",EDGE,"E118"),sQuery(id+"F0.wireOp",EDGE,"E119"),sQuery(id+"F0.wireOp",EDGE,"E120"),sQuery(id+"F0.wireOp",EDGE,"E121"),sQuery(id+"F0.wireOp",EDGE,"E122"),sQuery(id+"F0.wireOp",EDGE,"E123"),sQuery(id+"F0.wireOp",EDGE,"E124"),sQuery(id+"F0.wireOp",EDGE,"E125"),sQuery(id+"F0.wireOp",EDGE,"E126"),sQuery(id+"F0.wireOp",EDGE,"E127"),sQuery(id+"F0.wireOp",EDGE,"E128"),sQuery(id+"F0.wireOp",EDGE,"E129"),sQuery(id+"F0.wireOp",EDGE,"E130"),sQuery(id+"F0.wireOp",EDGE,"E131"),sQuery(id+"F0.wireOp",EDGE,"E132"),sQuery(id+"F0.wireOp",EDGE,"E133"),sQuery(id+"F0.wireOp",EDGE,"E134"),sQuery(id+"F0.wireOp",EDGE,"E135"),sQuery(id+"F0.wireOp",EDGE,"E136"),sQuery(id+"F0.wireOp",EDGE,"E137"),sQuery(id+"F0.wireOp",EDGE,"E138"),sQuery(id+"F0.wireOp",EDGE,"E139"),sQuery(id+"F0.wireOp",EDGE,"E140"),sQuery(id+"F0.wireOp",EDGE,"E141"),sQuery(id+"F0.wireOp",EDGE,"E142"),sQuery(id+"F0.wireOp",EDGE,"E143"),sQuery(id+"F0.wireOp",EDGE,"E144"),sQuery(id+"F0.wireOp",EDGE,"E145"),sQuery(id+"F0.wireOp",EDGE,"E146"),sQuery(id+"F0.wireOp",EDGE,"E147"),sQuery(id+"F0.wireOp",EDGE,"E148"),sQuery(id+"F0.wireOp",EDGE,"E149"),sQuery(id+"F0.wireOp",EDGE,"E150"),sQuery(id+"F0.wireOp",EDGE,"E151"),sQuery(id+"F0.wireOp",EDGE,"E152"),sQuery(id+"F0.wireOp",EDGE,"E153"),sQuery(id+"F0.wireOp",EDGE,"E154"),sQuery(id+"F0.wireOp",EDGE,"E155"),sQuery(id+"F0.wireOp",EDGE,"E156"),sQuery(id+"F0.wireOp",EDGE,"E157"),sQuery(id+"F0.wireOp",EDGE,"E158"),sQuery(id+"F0.wireOp",EDGE,"E159"),sQuery(id+"F0.wireOp",EDGE,"E160")])]});
            hole(context, id + "F4", {"style" : HoleStyle.C_SINK, "endStyle" : HoleEndStyle.THROUGH, "standardTappedOrClearance" : lookupTablePath({ "standard" : "ISO", "fit" : "Normal", "size" : "M3", "type" : "Clearance" }), "standardBlindInLast" : lookupTablePath({ "fit" : "Standard", "standard" : "ISO", "size" : "M3", "type" : "Clearance" }), "holeDiameter" : 3.3 * mm, "cSinkDiameter" : 6.72 * mm, "cSinkAngle" : 90 * degree, "isTappedThrough" : true, "tappedDepth" : 12 * mm, "tapClearance" : 3, "startFromSketch" : true, "locations" : qUnion([Q0, Q1, Q2, Q3, Q4, Q5, Q6, Q7, Q8, Q9, Q10, Q11, Q12, Q13, Q14, Q15, Q16, Q17, Q18, Q19, Q20]), "scope" : qUnion([Q21])});
        }
        {
            var Q0;
            Q0=makeQuery(id+"F1.opExtrude","CAP_FACE",FACE,{"disambiguationData":[OSD([sQuery(id+"F0.wireOp",EDGE,"E0"),sQuery(id+"F0.wireOp",EDGE,"E1"),sQuery(id+"F0.wireOp",EDGE,"E2"),sQuery(id+"F0.wireOp",EDGE,"E4"),sQuery(id+"F0.wireOp",EDGE,"E5"),sQuery(id+"F0.wireOp",EDGE,"E6"),sQuery(id+"F0.wireOp",EDGE,"E7"),sQuery(id+"F0.wireOp",EDGE,"E8"),sQuery(id+"F0.wireOp",EDGE,"E9"),sQuery(id+"F0.wireOp",EDGE,"E10"),sQuery(id+"F0.wireOp",EDGE,"E11"),sQuery(id+"F0.wireOp",EDGE,"E12"),sQuery(id+"F0.wireOp",EDGE,"E13"),sQuery(id+"F0.wireOp",EDGE,"E14"),sQuery(id+"F0.wireOp",EDGE,"E15"),sQuery(id+"F0.wireOp",EDGE,"E16"),sQuery(id+"F0.wireOp",EDGE,"E17"),sQuery(id+"F0.wireOp",EDGE,"E18"),sQuery(id+"F0.wireOp",EDGE,"E19"),sQuery(id+"F0.wireOp",EDGE,"E20"),sQuery(id+"F0.wireOp",EDGE,"E21"),sQuery(id+"F0.wireOp",EDGE,"E22"),sQuery(id+"F0.wireOp",EDGE,"E23"),sQuery(id+"F0.wireOp",EDGE,"E24"),sQuery(id+"F0.wireOp",EDGE,"E25"),sQuery(id+"F0.wireOp",EDGE,"E26"),sQuery(id+"F0.wireOp",EDGE,"E27"),sQuery(id+"F0.wireOp",EDGE,"E28"),sQuery(id+"F0.wireOp",EDGE,"E29"),sQuery(id+"F0.wireOp",EDGE,"E30"),sQuery(id+"F0.wireOp",EDGE,"E31"),sQuery(id+"F0.wireOp",EDGE,"E32"),sQuery(id+"F0.wireOp",EDGE,"E33"),sQuery(id+"F0.wireOp",EDGE,"E34"),sQuery(id+"F0.wireOp",EDGE,"E35"),sQuery(id+"F0.wireOp",EDGE,"E36"),sQuery(id+"F0.wireOp",EDGE,"E37"),sQuery(id+"F0.wireOp",EDGE,"E38"),sQuery(id+"F0.wireOp",EDGE,"E39"),sQuery(id+"F0.wireOp",EDGE,"E40"),sQuery(id+"F0.wireOp",EDGE,"E42"),sQuery(id+"F0.wireOp",EDGE,"E43"),sQuery(id+"F0.wireOp",EDGE,"E45"),sQuery(id+"F0.wireOp",EDGE,"E46"),sQuery(id+"F0.wireOp",EDGE,"E47"),sQuery(id+"F0.wireOp",EDGE,"E48"),sQuery(id+"F0.wireOp",EDGE,"E49"),sQuery(id+"F0.wireOp",EDGE,"E50"),sQuery(id+"F0.wireOp",EDGE,"E44"),sQuery(id+"F0.wireOp",EDGE,"E51"),sQuery(id+"F0.wireOp",EDGE,"E52"),sQuery(id+"F0.wireOp",EDGE,"E53"),sQuery(id+"F0.wireOp",EDGE,"E54"),sQuery(id+"F0.wireOp",EDGE,"E55"),sQuery(id+"F0.wireOp",EDGE,"E56"),sQuery(id+"F0.wireOp",EDGE,"E57"),sQuery(id+"F0.wireOp",EDGE,"E58"),sQuery(id+"F0.wireOp",EDGE,"E59"),sQuery(id+"F0.wireOp",EDGE,"E60"),sQuery(id+"F0.wireOp",EDGE,"E61"),sQuery(id+"F0.wireOp",EDGE,"E62"),sQuery(id+"F0.wireOp",EDGE,"E63"),sQuery(id+"F0.wireOp",EDGE,"E64"),sQuery(id+"F0.wireOp",EDGE,"E65"),sQuery(id+"F0.wireOp",EDGE,"E66"),sQuery(id+"F0.wireOp",EDGE,"E67"),sQuery(id+"F0.wireOp",EDGE,"E68"),sQuery(id+"F0.wireOp",EDGE,"E69"),sQuery(id+"F0.wireOp",EDGE,"E70"),sQuery(id+"F0.wireOp",EDGE,"E71"),sQuery(id+"F0.wireOp",EDGE,"E72"),sQuery(id+"F0.wireOp",EDGE,"E73"),sQuery(id+"F0.wireOp",EDGE,"E74"),sQuery(id+"F0.wireOp",EDGE,"E75"),sQuery(id+"F0.wireOp",EDGE,"E76"),sQuery(id+"F0.wireOp",EDGE,"E77"),sQuery(id+"F0.wireOp",EDGE,"E78"),sQuery(id+"F0.wireOp",EDGE,"E79"),sQuery(id+"F0.wireOp",EDGE,"E80"),sQuery(id+"F0.wireOp",EDGE,"E81"),sQuery(id+"F0.wireOp",EDGE,"E82"),sQuery(id+"F0.wireOp",EDGE,"E83"),sQuery(id+"F0.wireOp",EDGE,"E84"),sQuery(id+"F0.wireOp",EDGE,"E85"),sQuery(id+"F0.wireOp",EDGE,"E86"),sQuery(id+"F0.wireOp",EDGE,"E87"),sQuery(id+"F0.wireOp",EDGE,"E88"),sQuery(id+"F0.wireOp",EDGE,"E89"),sQuery(id+"F0.wireOp",EDGE,"E90"),sQuery(id+"F0.wireOp",EDGE,"E91"),sQuery(id+"F0.wireOp",EDGE,"E92"),sQuery(id+"F0.wireOp",EDGE,"E93"),sQuery(id+"F0.wireOp",EDGE,"E94"),sQuery(id+"F0.wireOp",EDGE,"E95"),sQuery(id+"F0.wireOp",EDGE,"E96"),sQuery(id+"F0.wireOp",EDGE,"E97"),sQuery(id+"F0.wireOp",EDGE,"E98"),sQuery(id+"F0.wireOp",EDGE,"E99"),sQuery(id+"F0.wireOp",EDGE,"E100"),sQuery(id+"F0.wireOp",EDGE,"E101"),sQuery(id+"F0.wireOp",EDGE,"E102"),sQuery(id+"F0.wireOp",EDGE,"E103"),sQuery(id+"F0.wireOp",EDGE,"E104"),sQuery(id+"F0.wireOp",EDGE,"E105"),sQuery(id+"F0.wireOp",EDGE,"E106"),sQuery(id+"F0.wireOp",EDGE,"E107"),sQuery(id+"F0.wireOp",EDGE,"E108"),sQuery(id+"F0.wireOp",EDGE,"E109"),sQuery(id+"F0.wireOp",EDGE,"E110"),sQuery(id+"F0.wireOp",EDGE,"E111"),sQuery(id+"F0.wireOp",EDGE,"E112"),sQuery(id+"F0.wireOp",EDGE,"E113"),sQuery(id+"F0.wireOp",EDGE,"E114"),sQuery(id+"F0.wireOp",EDGE,"E115"),sQuery(id+"F0.wireOp",EDGE,"E116"),sQuery(id+"F0.wireOp",EDGE,"E117"),sQuery(id+"F0.wireOp",EDGE,"E118"),sQuery(id+"F0.wireOp",EDGE,"E119"),sQuery(id+"F0.wireOp",EDGE,"E120"),sQuery(id+"F0.wireOp",EDGE,"E121"),sQuery(id+"F0.wireOp",EDGE,"E122"),sQuery(id+"F0.wireOp",EDGE,"E123"),sQuery(id+"F0.wireOp",EDGE,"E124"),sQuery(id+"F0.wireOp",EDGE,"E125"),sQuery(id+"F0.wireOp",EDGE,"E126"),sQuery(id+"F0.wireOp",EDGE,"E127"),sQuery(id+"F0.wireOp",EDGE,"E128"),sQuery(id+"F0.wireOp",EDGE,"E129"),sQuery(id+"F0.wireOp",EDGE,"E130"),sQuery(id+"F0.wireOp",EDGE,"E131"),sQuery(id+"F0.wireOp",EDGE,"E132"),sQuery(id+"F0.wireOp",EDGE,"E133"),sQuery(id+"F0.wireOp",EDGE,"E134"),sQuery(id+"F0.wireOp",EDGE,"E135"),sQuery(id+"F0.wireOp",EDGE,"E136"),sQuery(id+"F0.wireOp",EDGE,"E137"),sQuery(id+"F0.wireOp",EDGE,"E138"),sQuery(id+"F0.wireOp",EDGE,"E139"),sQuery(id+"F0.wireOp",EDGE,"E140"),sQuery(id+"F0.wireOp",EDGE,"E141"),sQuery(id+"F0.wireOp",EDGE,"E142"),sQuery(id+"F0.wireOp",EDGE,"E143"),sQuery(id+"F0.wireOp",EDGE,"E144"),sQuery(id+"F0.wireOp",EDGE,"E145"),sQuery(id+"F0.wireOp",EDGE,"E146"),sQuery(id+"F0.wireOp",EDGE,"E147"),sQuery(id+"F0.wireOp",EDGE,"E148"),sQuery(id+"F0.wireOp",EDGE,"E149"),sQuery(id+"F0.wireOp",EDGE,"E150"),sQuery(id+"F0.wireOp",EDGE,"E151"),sQuery(id+"F0.wireOp",EDGE,"E152"),sQuery(id+"F0.wireOp",EDGE,"E153"),sQuery(id+"F0.wireOp",EDGE,"E154"),sQuery(id+"F0.wireOp",EDGE,"E155"),sQuery(id+"F0.wireOp",EDGE,"E156"),sQuery(id+"F0.wireOp",EDGE,"E157"),sQuery(id+"F0.wireOp",EDGE,"E158"),sQuery(id+"F0.wireOp",EDGE,"E159"),sQuery(id+"F0.wireOp",EDGE,"E160")])],"isStart":false});
            var sketch = newSketch(context, id + "F5", { "sketchPlane" : qUnion([Q0])});
            skCircle(sketch, "E185", {"center": v(69, 77.5) * mm, "radius": 3.5 * mm, "construction": true});
            skLineSegment(sketch, "E186.bottom", {"start": v(65.5, 77.74) * mm, "end": v(69, 77.74) * mm, "construction": true});
            skLineSegment(sketch, "E186.top", {"start": v(65.5, 81) * mm, "end": v(69, 81) * mm});
            skLineSegment(sketch, "E186.left", {"start": v(65.5, 77.74) * mm, "end": v(65.5, 81) * mm});
            skLineSegment(sketch, "E186.right", {"start": v(69, 77.74) * mm, "end": v(69, 81) * mm, "construction": true});
            skLineSegment(sketch, "E187.bottom", {"start": v(65.5, 81) * mm, "end": v(75.5, 81) * mm});
            skLineSegment(sketch, "E187.top", {"start": v(65.5, 74) * mm, "end": v(75.5, 74) * mm});
            skLineSegment(sketch, "E187.left", {"start": v(65.5, 81) * mm, "end": v(65.5, 74) * mm, "construction": true});
            skLineSegment(sketch, "E187.right", {"start": v(75.5, 81) * mm, "end": v(75.5, 74) * mm});
            skPoint(sketch, "E188", {"position": v(15.37, 77.5) * mm});
            skLineSegment(sketch, "E189.bottom", {"start": v(75.5, 81) * mm, "end": v(-44.5, 81) * mm});
            skLineSegment(sketch, "E189.top", {"start": v(75.5, 74) * mm, "end": v(-44.5, 74) * mm});
            skLineSegment(sketch, "E189.right", {"start": v(-44.5, 81) * mm, "end": v(-44.5, 74) * mm});
            skPoint(sketch, "E190.0", {"position": v(-40.63, 77.5) * mm});
            skSolve(sketch);
        }
        {
            var Q0;
            {var subQ15=sQuery(id+"F5.wireOp",EDGE,"E187.right");Q0=makeQuery(id+"F5.imprint","IMPRINT",FACE,{"disambiguationData":[TD([[makeQuery(id+"F5.imprint","IMPRINT",EDGE,{"derivedFrom":subQ15}),1.0]])]});}
            var Q1;
            {var subQ0=sQuery(id+"F5.wireOp",EDGE,"E189.top");var subQ1=makeQuery(id+"F1.opExtrude","CAP_EDGE",EDGE,{"disambiguationData":[OSD([sQuery(id+"F0.wireOp",EDGE,"E134")])],"isStart":false});var subQ2=makeQuery(id+"F5.imprint","INTERSECT",VERTEX,{"disambiguationData":[OD(0.0)],"derivedFrom":[subQ1,subQ0]});var subQ3=makeQuery(id+"F5.imprint","INTERSECT",VERTEX,{"disambiguationData":[OD(1.0)],"derivedFrom":[subQ1,subQ0]});Q1=makeQuery(id+"F5.imprint","IMPRINT",FACE,{"disambiguationData":[TD([[makeQuery(id+"F5.imprint","IMPRINT",EDGE,{"disambiguationData":[TD([[subQ2,-1.0],[subQ3,1.0]])],"derivedFrom":subQ0}),-1.0]])]});}
            var Q2;
            Q2=makeQuery(id+"F5.imprint","IMPRINT",FACE,{"disambiguationData":[TD([[makeQuery(id+"F5.imprint","IMPRINT",EDGE,{"derivedFrom":makeQuery(id+"F4.hole-19.boolean.opBoolean","INTERSECT",EDGE,{"derivedFrom":[makeQuery(id+"F1.opExtrude","CAP_FACE",FACE,{"disambiguationData":[OSD([sQuery(id+"F0.wireOp",EDGE,"E0"),sQuery(id+"F0.wireOp",EDGE,"E1"),sQuery(id+"F0.wireOp",EDGE,"E2"),sQuery(id+"F0.wireOp",EDGE,"E4"),sQuery(id+"F0.wireOp",EDGE,"E5"),sQuery(id+"F0.wireOp",EDGE,"E6"),sQuery(id+"F0.wireOp",EDGE,"E7"),sQuery(id+"F0.wireOp",EDGE,"E8"),sQuery(id+"F0.wireOp",EDGE,"E9"),sQuery(id+"F0.wireOp",EDGE,"E10"),sQuery(id+"F0.wireOp",EDGE,"E11"),sQuery(id+"F0.wireOp",EDGE,"E12"),sQuery(id+"F0.wireOp",EDGE,"E13"),sQuery(id+"F0.wireOp",EDGE,"E14"),sQuery(id+"F0.wireOp",EDGE,"E15"),sQuery(id+"F0.wireOp",EDGE,"E16"),sQuery(id+"F0.wireOp",EDGE,"E17"),sQuery(id+"F0.wireOp",EDGE,"E18"),sQuery(id+"F0.wireOp",EDGE,"E19"),sQuery(id+"F0.wireOp",EDGE,"E20"),sQuery(id+"F0.wireOp",EDGE,"E21"),sQuery(id+"F0.wireOp",EDGE,"E22"),sQuery(id+"F0.wireOp",EDGE,"E23"),sQuery(id+"F0.wireOp",EDGE,"E24"),sQuery(id+"F0.wireOp",EDGE,"E25"),sQuery(id+"F0.wireOp",EDGE,"E26"),sQuery(id+"F0.wireOp",EDGE,"E27"),sQuery(id+"F0.wireOp",EDGE,"E28"),sQuery(id+"F0.wireOp",EDGE,"E29"),sQuery(id+"F0.wireOp",EDGE,"E30"),sQuery(id+"F0.wireOp",EDGE,"E31"),sQuery(id+"F0.wireOp",EDGE,"E32"),sQuery(id+"F0.wireOp",EDGE,"E33"),sQuery(id+"F0.wireOp",EDGE,"E34"),sQuery(id+"F0.wireOp",EDGE,"E35"),sQuery(id+"F0.wireOp",EDGE,"E36"),sQuery(id+"F0.wireOp",EDGE,"E37"),sQuery(id+"F0.wireOp",EDGE,"E38"),sQuery(id+"F0.wireOp",EDGE,"E39"),sQuery(id+"F0.wireOp",EDGE,"E40"),sQuery(id+"F0.wireOp",EDGE,"E42"),sQuery(id+"F0.wireOp",EDGE,"E43"),sQuery(id+"F0.wireOp",EDGE,"E45"),sQuery(id+"F0.wireOp",EDGE,"E46"),sQuery(id+"F0.wireOp",EDGE,"E47"),sQuery(id+"F0.wireOp",EDGE,"E48"),sQuery(id+"F0.wireOp",EDGE,"E49"),sQuery(id+"F0.wireOp",EDGE,"E50"),sQuery(id+"F0.wireOp",EDGE,"E44"),sQuery(id+"F0.wireOp",EDGE,"E51"),sQuery(id+"F0.wireOp",EDGE,"E52"),sQuery(id+"F0.wireOp",EDGE,"E53"),sQuery(id+"F0.wireOp",EDGE,"E54"),sQuery(id+"F0.wireOp",EDGE,"E55"),sQuery(id+"F0.wireOp",EDGE,"E56"),sQuery(id+"F0.wireOp",EDGE,"E57"),sQuery(id+"F0.wireOp",EDGE,"E58"),sQuery(id+"F0.wireOp",EDGE,"E59"),sQuery(id+"F0.wireOp",EDGE,"E60"),sQuery(id+"F0.wireOp",EDGE,"E61"),sQuery(id+"F0.wireOp",EDGE,"E62"),sQuery(id+"F0.wireOp",EDGE,"E63"),sQuery(id+"F0.wireOp",EDGE,"E64"),sQuery(id+"F0.wireOp",EDGE,"E65"),sQuery(id+"F0.wireOp",EDGE,"E66"),sQuery(id+"F0.wireOp",EDGE,"E67"),sQuery(id+"F0.wireOp",EDGE,"E68"),sQuery(id+"F0.wireOp",EDGE,"E69"),sQuery(id+"F0.wireOp",EDGE,"E70"),sQuery(id+"F0.wireOp",EDGE,"E71"),sQuery(id+"F0.wireOp",EDGE,"E72"),sQuery(id+"F0.wireOp",EDGE,"E73"),sQuery(id+"F0.wireOp",EDGE,"E74"),sQuery(id+"F0.wireOp",EDGE,"E75"),sQuery(id+"F0.wireOp",EDGE,"E76"),sQuery(id+"F0.wireOp",EDGE,"E77"),sQuery(id+"F0.wireOp",EDGE,"E78"),sQuery(id+"F0.wireOp",EDGE,"E79"),sQuery(id+"F0.wireOp",EDGE,"E80"),sQuery(id+"F0.wireOp",EDGE,"E81"),sQuery(id+"F0.wireOp",EDGE,"E82"),sQuery(id+"F0.wireOp",EDGE,"E83"),sQuery(id+"F0.wireOp",EDGE,"E84"),sQuery(id+"F0.wireOp",EDGE,"E85"),sQuery(id+"F0.wireOp",EDGE,"E86"),sQuery(id+"F0.wireOp",EDGE,"E87"),sQuery(id+"F0.wireOp",EDGE,"E88"),sQuery(id+"F0.wireOp",EDGE,"E89"),sQuery(id+"F0.wireOp",EDGE,"E90"),sQuery(id+"F0.wireOp",EDGE,"E91"),sQuery(id+"F0.wireOp",EDGE,"E92"),sQuery(id+"F0.wireOp",EDGE,"E93"),sQuery(id+"F0.wireOp",EDGE,"E94"),sQuery(id+"F0.wireOp",EDGE,"E95"),sQuery(id+"F0.wireOp",EDGE,"E96"),sQuery(id+"F0.wireOp",EDGE,"E97"),sQuery(id+"F0.wireOp",EDGE,"E98"),sQuery(id+"F0.wireOp",EDGE,"E99"),sQuery(id+"F0.wireOp",EDGE,"E100"),sQuery(id+"F0.wireOp",EDGE,"E101"),sQuery(id+"F0.wireOp",EDGE,"E102"),sQuery(id+"F0.wireOp",EDGE,"E103"),sQuery(id+"F0.wireOp",EDGE,"E104"),sQuery(id+"F0.wireOp",EDGE,"E105"),sQuery(id+"F0.wireOp",EDGE,"E106"),sQuery(id+"F0.wireOp",EDGE,"E107"),sQuery(id+"F0.wireOp",EDGE,"E108"),sQuery(id+"F0.wireOp",EDGE,"E109"),sQuery(id+"F0.wireOp",EDGE,"E110"),sQuery(id+"F0.wireOp",EDGE,"E111"),sQuery(id+"F0.wireOp",EDGE,"E112"),sQuery(id+"F0.wireOp",EDGE,"E113"),sQuery(id+"F0.wireOp",EDGE,"E114"),sQuery(id+"F0.wireOp",EDGE,"E115"),sQuery(id+"F0.wireOp",EDGE,"E116"),sQuery(id+"F0.wireOp",EDGE,"E117"),sQuery(id+"F0.wireOp",EDGE,"E118"),sQuery(id+"F0.wireOp",EDGE,"E119"),sQuery(id+"F0.wireOp",EDGE,"E120"),sQuery(id+"F0.wireOp",EDGE,"E121"),sQuery(id+"F0.wireOp",EDGE,"E122"),sQuery(id+"F0.wireOp",EDGE,"E123"),sQuery(id+"F0.wireOp",EDGE,"E124"),sQuery(id+"F0.wireOp",EDGE,"E125"),sQuery(id+"F0.wireOp",EDGE,"E126"),sQuery(id+"F0.wireOp",EDGE,"E127"),sQuery(id+"F0.wireOp",EDGE,"E128"),sQuery(id+"F0.wireOp",EDGE,"E129"),sQuery(id+"F0.wireOp",EDGE,"E130"),sQuery(id+"F0.wireOp",EDGE,"E131"),sQuery(id+"F0.wireOp",EDGE,"E132"),sQuery(id+"F0.wireOp",EDGE,"E133"),sQuery(id+"F0.wireOp",EDGE,"E134"),sQuery(id+"F0.wireOp",EDGE,"E135"),sQuery(id+"F0.wireOp",EDGE,"E136"),sQuery(id+"F0.wireOp",EDGE,"E137"),sQuery(id+"F0.wireOp",EDGE,"E138"),sQuery(id+"F0.wireOp",EDGE,"E139"),sQuery(id+"F0.wireOp",EDGE,"E140"),sQuery(id+"F0.wireOp",EDGE,"E141"),sQuery(id+"F0.wireOp",EDGE,"E142"),sQuery(id+"F0.wireOp",EDGE,"E143"),sQuery(id+"F0.wireOp",EDGE,"E144"),sQuery(id+"F0.wireOp",EDGE,"E145"),sQuery(id+"F0.wireOp",EDGE,"E146"),sQuery(id+"F0.wireOp",EDGE,"E147"),sQuery(id+"F0.wireOp",EDGE,"E148"),sQuery(id+"F0.wireOp",EDGE,"E149"),sQuery(id+"F0.wireOp",EDGE,"E150"),sQuery(id+"F0.wireOp",EDGE,"E151"),sQuery(id+"F0.wireOp",EDGE,"E152"),sQuery(id+"F0.wireOp",EDGE,"E153"),sQuery(id+"F0.wireOp",EDGE,"E154"),sQuery(id+"F0.wireOp",EDGE,"E155"),sQuery(id+"F0.wireOp",EDGE,"E156"),sQuery(id+"F0.wireOp",EDGE,"E157"),sQuery(id+"F0.wireOp",EDGE,"E158"),sQuery(id+"F0.wireOp",EDGE,"E159"),sQuery(id+"F0.wireOp",EDGE,"E160")])],"isStart":false}),makeQuery(id+"F4.hole-19.opRevolve","SWEPT_FACE",FACE,{"disambiguationData":[OSD([sQuery(id+"F4.hole-19.sketch.wireOp",EDGE,"core_line_2")])]})]})}),1.0]])]});
            var Q3;
            Q3=makeQuery(id+"F5.imprint","IMPRINT",FACE,{"disambiguationData":[TD([[makeQuery(id+"F5.imprint","IMPRINT",EDGE,{"derivedFrom":makeQuery(id+"F4.hole-20.boolean.opBoolean","INTERSECT",EDGE,{"derivedFrom":[makeQuery(id+"F1.opExtrude","CAP_FACE",FACE,{"disambiguationData":[OSD([sQuery(id+"F0.wireOp",EDGE,"E0"),sQuery(id+"F0.wireOp",EDGE,"E1"),sQuery(id+"F0.wireOp",EDGE,"E2"),sQuery(id+"F0.wireOp",EDGE,"E4"),sQuery(id+"F0.wireOp",EDGE,"E5"),sQuery(id+"F0.wireOp",EDGE,"E6"),sQuery(id+"F0.wireOp",EDGE,"E7"),sQuery(id+"F0.wireOp",EDGE,"E8"),sQuery(id+"F0.wireOp",EDGE,"E9"),sQuery(id+"F0.wireOp",EDGE,"E10"),sQuery(id+"F0.wireOp",EDGE,"E11"),sQuery(id+"F0.wireOp",EDGE,"E12"),sQuery(id+"F0.wireOp",EDGE,"E13"),sQuery(id+"F0.wireOp",EDGE,"E14"),sQuery(id+"F0.wireOp",EDGE,"E15"),sQuery(id+"F0.wireOp",EDGE,"E16"),sQuery(id+"F0.wireOp",EDGE,"E17"),sQuery(id+"F0.wireOp",EDGE,"E18"),sQuery(id+"F0.wireOp",EDGE,"E19"),sQuery(id+"F0.wireOp",EDGE,"E20"),sQuery(id+"F0.wireOp",EDGE,"E21"),sQuery(id+"F0.wireOp",EDGE,"E22"),sQuery(id+"F0.wireOp",EDGE,"E23"),sQuery(id+"F0.wireOp",EDGE,"E24"),sQuery(id+"F0.wireOp",EDGE,"E25"),sQuery(id+"F0.wireOp",EDGE,"E26"),sQuery(id+"F0.wireOp",EDGE,"E27"),sQuery(id+"F0.wireOp",EDGE,"E28"),sQuery(id+"F0.wireOp",EDGE,"E29"),sQuery(id+"F0.wireOp",EDGE,"E30"),sQuery(id+"F0.wireOp",EDGE,"E31"),sQuery(id+"F0.wireOp",EDGE,"E32"),sQuery(id+"F0.wireOp",EDGE,"E33"),sQuery(id+"F0.wireOp",EDGE,"E34"),sQuery(id+"F0.wireOp",EDGE,"E35"),sQuery(id+"F0.wireOp",EDGE,"E36"),sQuery(id+"F0.wireOp",EDGE,"E37"),sQuery(id+"F0.wireOp",EDGE,"E38"),sQuery(id+"F0.wireOp",EDGE,"E39"),sQuery(id+"F0.wireOp",EDGE,"E40"),sQuery(id+"F0.wireOp",EDGE,"E42"),sQuery(id+"F0.wireOp",EDGE,"E43"),sQuery(id+"F0.wireOp",EDGE,"E45"),sQuery(id+"F0.wireOp",EDGE,"E46"),sQuery(id+"F0.wireOp",EDGE,"E47"),sQuery(id+"F0.wireOp",EDGE,"E48"),sQuery(id+"F0.wireOp",EDGE,"E49"),sQuery(id+"F0.wireOp",EDGE,"E50"),sQuery(id+"F0.wireOp",EDGE,"E44"),sQuery(id+"F0.wireOp",EDGE,"E51"),sQuery(id+"F0.wireOp",EDGE,"E52"),sQuery(id+"F0.wireOp",EDGE,"E53"),sQuery(id+"F0.wireOp",EDGE,"E54"),sQuery(id+"F0.wireOp",EDGE,"E55"),sQuery(id+"F0.wireOp",EDGE,"E56"),sQuery(id+"F0.wireOp",EDGE,"E57"),sQuery(id+"F0.wireOp",EDGE,"E58"),sQuery(id+"F0.wireOp",EDGE,"E59"),sQuery(id+"F0.wireOp",EDGE,"E60"),sQuery(id+"F0.wireOp",EDGE,"E61"),sQuery(id+"F0.wireOp",EDGE,"E62"),sQuery(id+"F0.wireOp",EDGE,"E63"),sQuery(id+"F0.wireOp",EDGE,"E64"),sQuery(id+"F0.wireOp",EDGE,"E65"),sQuery(id+"F0.wireOp",EDGE,"E66"),sQuery(id+"F0.wireOp",EDGE,"E67"),sQuery(id+"F0.wireOp",EDGE,"E68"),sQuery(id+"F0.wireOp",EDGE,"E69"),sQuery(id+"F0.wireOp",EDGE,"E70"),sQuery(id+"F0.wireOp",EDGE,"E71"),sQuery(id+"F0.wireOp",EDGE,"E72"),sQuery(id+"F0.wireOp",EDGE,"E73"),sQuery(id+"F0.wireOp",EDGE,"E74"),sQuery(id+"F0.wireOp",EDGE,"E75"),sQuery(id+"F0.wireOp",EDGE,"E76"),sQuery(id+"F0.wireOp",EDGE,"E77"),sQuery(id+"F0.wireOp",EDGE,"E78"),sQuery(id+"F0.wireOp",EDGE,"E79"),sQuery(id+"F0.wireOp",EDGE,"E80"),sQuery(id+"F0.wireOp",EDGE,"E81"),sQuery(id+"F0.wireOp",EDGE,"E82"),sQuery(id+"F0.wireOp",EDGE,"E83"),sQuery(id+"F0.wireOp",EDGE,"E84"),sQuery(id+"F0.wireOp",EDGE,"E85"),sQuery(id+"F0.wireOp",EDGE,"E86"),sQuery(id+"F0.wireOp",EDGE,"E87"),sQuery(id+"F0.wireOp",EDGE,"E88"),sQuery(id+"F0.wireOp",EDGE,"E89"),sQuery(id+"F0.wireOp",EDGE,"E90"),sQuery(id+"F0.wireOp",EDGE,"E91"),sQuery(id+"F0.wireOp",EDGE,"E92"),sQuery(id+"F0.wireOp",EDGE,"E93"),sQuery(id+"F0.wireOp",EDGE,"E94"),sQuery(id+"F0.wireOp",EDGE,"E95"),sQuery(id+"F0.wireOp",EDGE,"E96"),sQuery(id+"F0.wireOp",EDGE,"E97"),sQuery(id+"F0.wireOp",EDGE,"E98"),sQuery(id+"F0.wireOp",EDGE,"E99"),sQuery(id+"F0.wireOp",EDGE,"E100"),sQuery(id+"F0.wireOp",EDGE,"E101"),sQuery(id+"F0.wireOp",EDGE,"E102"),sQuery(id+"F0.wireOp",EDGE,"E103"),sQuery(id+"F0.wireOp",EDGE,"E104"),sQuery(id+"F0.wireOp",EDGE,"E105"),sQuery(id+"F0.wireOp",EDGE,"E106"),sQuery(id+"F0.wireOp",EDGE,"E107"),sQuery(id+"F0.wireOp",EDGE,"E108"),sQuery(id+"F0.wireOp",EDGE,"E109"),sQuery(id+"F0.wireOp",EDGE,"E110"),sQuery(id+"F0.wireOp",EDGE,"E111"),sQuery(id+"F0.wireOp",EDGE,"E112"),sQuery(id+"F0.wireOp",EDGE,"E113"),sQuery(id+"F0.wireOp",EDGE,"E114"),sQuery(id+"F0.wireOp",EDGE,"E115"),sQuery(id+"F0.wireOp",EDGE,"E116"),sQuery(id+"F0.wireOp",EDGE,"E117"),sQuery(id+"F0.wireOp",EDGE,"E118"),sQuery(id+"F0.wireOp",EDGE,"E119"),sQuery(id+"F0.wireOp",EDGE,"E120"),sQuery(id+"F0.wireOp",EDGE,"E121"),sQuery(id+"F0.wireOp",EDGE,"E122"),sQuery(id+"F0.wireOp",EDGE,"E123"),sQuery(id+"F0.wireOp",EDGE,"E124"),sQuery(id+"F0.wireOp",EDGE,"E125"),sQuery(id+"F0.wireOp",EDGE,"E126"),sQuery(id+"F0.wireOp",EDGE,"E127"),sQuery(id+"F0.wireOp",EDGE,"E128"),sQuery(id+"F0.wireOp",EDGE,"E129"),sQuery(id+"F0.wireOp",EDGE,"E130"),sQuery(id+"F0.wireOp",EDGE,"E131"),sQuery(id+"F0.wireOp",EDGE,"E132"),sQuery(id+"F0.wireOp",EDGE,"E133"),sQuery(id+"F0.wireOp",EDGE,"E134"),sQuery(id+"F0.wireOp",EDGE,"E135"),sQuery(id+"F0.wireOp",EDGE,"E136"),sQuery(id+"F0.wireOp",EDGE,"E137"),sQuery(id+"F0.wireOp",EDGE,"E138"),sQuery(id+"F0.wireOp",EDGE,"E139"),sQuery(id+"F0.wireOp",EDGE,"E140"),sQuery(id+"F0.wireOp",EDGE,"E141"),sQuery(id+"F0.wireOp",EDGE,"E142"),sQuery(id+"F0.wireOp",EDGE,"E143"),sQuery(id+"F0.wireOp",EDGE,"E144"),sQuery(id+"F0.wireOp",EDGE,"E145"),sQuery(id+"F0.wireOp",EDGE,"E146"),sQuery(id+"F0.wireOp",EDGE,"E147"),sQuery(id+"F0.wireOp",EDGE,"E148"),sQuery(id+"F0.wireOp",EDGE,"E149"),sQuery(id+"F0.wireOp",EDGE,"E150"),sQuery(id+"F0.wireOp",EDGE,"E151"),sQuery(id+"F0.wireOp",EDGE,"E152"),sQuery(id+"F0.wireOp",EDGE,"E153"),sQuery(id+"F0.wireOp",EDGE,"E154"),sQuery(id+"F0.wireOp",EDGE,"E155"),sQuery(id+"F0.wireOp",EDGE,"E156"),sQuery(id+"F0.wireOp",EDGE,"E157"),sQuery(id+"F0.wireOp",EDGE,"E158"),sQuery(id+"F0.wireOp",EDGE,"E159"),sQuery(id+"F0.wireOp",EDGE,"E160")])],"isStart":false}),makeQuery(id+"F4.hole-20.opRevolve","SWEPT_FACE",FACE,{"disambiguationData":[OSD([sQuery(id+"F4.hole-20.sketch.wireOp",EDGE,"core_line_2")])]})]})}),1.0]])]});
            var Q4;
            Q4=makeQuery(id+"F5.imprint","IMPRINT",FACE,{"disambiguationData":[TD([[makeQuery(id+"F5.imprint","IMPRINT",EDGE,{"derivedFrom":makeQuery(id+"F4.hole-18.boolean.opBoolean","INTERSECT",EDGE,{"derivedFrom":[makeQuery(id+"F1.opExtrude","CAP_FACE",FACE,{"disambiguationData":[OSD([sQuery(id+"F0.wireOp",EDGE,"E0"),sQuery(id+"F0.wireOp",EDGE,"E1"),sQuery(id+"F0.wireOp",EDGE,"E2"),sQuery(id+"F0.wireOp",EDGE,"E4"),sQuery(id+"F0.wireOp",EDGE,"E5"),sQuery(id+"F0.wireOp",EDGE,"E6"),sQuery(id+"F0.wireOp",EDGE,"E7"),sQuery(id+"F0.wireOp",EDGE,"E8"),sQuery(id+"F0.wireOp",EDGE,"E9"),sQuery(id+"F0.wireOp",EDGE,"E10"),sQuery(id+"F0.wireOp",EDGE,"E11"),sQuery(id+"F0.wireOp",EDGE,"E12"),sQuery(id+"F0.wireOp",EDGE,"E13"),sQuery(id+"F0.wireOp",EDGE,"E14"),sQuery(id+"F0.wireOp",EDGE,"E15"),sQuery(id+"F0.wireOp",EDGE,"E16"),sQuery(id+"F0.wireOp",EDGE,"E17"),sQuery(id+"F0.wireOp",EDGE,"E18"),sQuery(id+"F0.wireOp",EDGE,"E19"),sQuery(id+"F0.wireOp",EDGE,"E20"),sQuery(id+"F0.wireOp",EDGE,"E21"),sQuery(id+"F0.wireOp",EDGE,"E22"),sQuery(id+"F0.wireOp",EDGE,"E23"),sQuery(id+"F0.wireOp",EDGE,"E24"),sQuery(id+"F0.wireOp",EDGE,"E25"),sQuery(id+"F0.wireOp",EDGE,"E26"),sQuery(id+"F0.wireOp",EDGE,"E27"),sQuery(id+"F0.wireOp",EDGE,"E28"),sQuery(id+"F0.wireOp",EDGE,"E29"),sQuery(id+"F0.wireOp",EDGE,"E30"),sQuery(id+"F0.wireOp",EDGE,"E31"),sQuery(id+"F0.wireOp",EDGE,"E32"),sQuery(id+"F0.wireOp",EDGE,"E33"),sQuery(id+"F0.wireOp",EDGE,"E34"),sQuery(id+"F0.wireOp",EDGE,"E35"),sQuery(id+"F0.wireOp",EDGE,"E36"),sQuery(id+"F0.wireOp",EDGE,"E37"),sQuery(id+"F0.wireOp",EDGE,"E38"),sQuery(id+"F0.wireOp",EDGE,"E39"),sQuery(id+"F0.wireOp",EDGE,"E40"),sQuery(id+"F0.wireOp",EDGE,"E42"),sQuery(id+"F0.wireOp",EDGE,"E43"),sQuery(id+"F0.wireOp",EDGE,"E45"),sQuery(id+"F0.wireOp",EDGE,"E46"),sQuery(id+"F0.wireOp",EDGE,"E47"),sQuery(id+"F0.wireOp",EDGE,"E48"),sQuery(id+"F0.wireOp",EDGE,"E49"),sQuery(id+"F0.wireOp",EDGE,"E50"),sQuery(id+"F0.wireOp",EDGE,"E44"),sQuery(id+"F0.wireOp",EDGE,"E51"),sQuery(id+"F0.wireOp",EDGE,"E52"),sQuery(id+"F0.wireOp",EDGE,"E53"),sQuery(id+"F0.wireOp",EDGE,"E54"),sQuery(id+"F0.wireOp",EDGE,"E55"),sQuery(id+"F0.wireOp",EDGE,"E56"),sQuery(id+"F0.wireOp",EDGE,"E57"),sQuery(id+"F0.wireOp",EDGE,"E58"),sQuery(id+"F0.wireOp",EDGE,"E59"),sQuery(id+"F0.wireOp",EDGE,"E60"),sQuery(id+"F0.wireOp",EDGE,"E61"),sQuery(id+"F0.wireOp",EDGE,"E62"),sQuery(id+"F0.wireOp",EDGE,"E63"),sQuery(id+"F0.wireOp",EDGE,"E64"),sQuery(id+"F0.wireOp",EDGE,"E65"),sQuery(id+"F0.wireOp",EDGE,"E66"),sQuery(id+"F0.wireOp",EDGE,"E67"),sQuery(id+"F0.wireOp",EDGE,"E68"),sQuery(id+"F0.wireOp",EDGE,"E69"),sQuery(id+"F0.wireOp",EDGE,"E70"),sQuery(id+"F0.wireOp",EDGE,"E71"),sQuery(id+"F0.wireOp",EDGE,"E72"),sQuery(id+"F0.wireOp",EDGE,"E73"),sQuery(id+"F0.wireOp",EDGE,"E74"),sQuery(id+"F0.wireOp",EDGE,"E75"),sQuery(id+"F0.wireOp",EDGE,"E76"),sQuery(id+"F0.wireOp",EDGE,"E77"),sQuery(id+"F0.wireOp",EDGE,"E78"),sQuery(id+"F0.wireOp",EDGE,"E79"),sQuery(id+"F0.wireOp",EDGE,"E80"),sQuery(id+"F0.wireOp",EDGE,"E81"),sQuery(id+"F0.wireOp",EDGE,"E82"),sQuery(id+"F0.wireOp",EDGE,"E83"),sQuery(id+"F0.wireOp",EDGE,"E84"),sQuery(id+"F0.wireOp",EDGE,"E85"),sQuery(id+"F0.wireOp",EDGE,"E86"),sQuery(id+"F0.wireOp",EDGE,"E87"),sQuery(id+"F0.wireOp",EDGE,"E88"),sQuery(id+"F0.wireOp",EDGE,"E89"),sQuery(id+"F0.wireOp",EDGE,"E90"),sQuery(id+"F0.wireOp",EDGE,"E91"),sQuery(id+"F0.wireOp",EDGE,"E92"),sQuery(id+"F0.wireOp",EDGE,"E93"),sQuery(id+"F0.wireOp",EDGE,"E94"),sQuery(id+"F0.wireOp",EDGE,"E95"),sQuery(id+"F0.wireOp",EDGE,"E96"),sQuery(id+"F0.wireOp",EDGE,"E97"),sQuery(id+"F0.wireOp",EDGE,"E98"),sQuery(id+"F0.wireOp",EDGE,"E99"),sQuery(id+"F0.wireOp",EDGE,"E100"),sQuery(id+"F0.wireOp",EDGE,"E101"),sQuery(id+"F0.wireOp",EDGE,"E102"),sQuery(id+"F0.wireOp",EDGE,"E103"),sQuery(id+"F0.wireOp",EDGE,"E104"),sQuery(id+"F0.wireOp",EDGE,"E105"),sQuery(id+"F0.wireOp",EDGE,"E106"),sQuery(id+"F0.wireOp",EDGE,"E107"),sQuery(id+"F0.wireOp",EDGE,"E108"),sQuery(id+"F0.wireOp",EDGE,"E109"),sQuery(id+"F0.wireOp",EDGE,"E110"),sQuery(id+"F0.wireOp",EDGE,"E111"),sQuery(id+"F0.wireOp",EDGE,"E112"),sQuery(id+"F0.wireOp",EDGE,"E113"),sQuery(id+"F0.wireOp",EDGE,"E114"),sQuery(id+"F0.wireOp",EDGE,"E115"),sQuery(id+"F0.wireOp",EDGE,"E116"),sQuery(id+"F0.wireOp",EDGE,"E117"),sQuery(id+"F0.wireOp",EDGE,"E118"),sQuery(id+"F0.wireOp",EDGE,"E119"),sQuery(id+"F0.wireOp",EDGE,"E120"),sQuery(id+"F0.wireOp",EDGE,"E121"),sQuery(id+"F0.wireOp",EDGE,"E122"),sQuery(id+"F0.wireOp",EDGE,"E123"),sQuery(id+"F0.wireOp",EDGE,"E124"),sQuery(id+"F0.wireOp",EDGE,"E125"),sQuery(id+"F0.wireOp",EDGE,"E126"),sQuery(id+"F0.wireOp",EDGE,"E127"),sQuery(id+"F0.wireOp",EDGE,"E128"),sQuery(id+"F0.wireOp",EDGE,"E129"),sQuery(id+"F0.wireOp",EDGE,"E130"),sQuery(id+"F0.wireOp",EDGE,"E131"),sQuery(id+"F0.wireOp",EDGE,"E132"),sQuery(id+"F0.wireOp",EDGE,"E133"),sQuery(id+"F0.wireOp",EDGE,"E134"),sQuery(id+"F0.wireOp",EDGE,"E135"),sQuery(id+"F0.wireOp",EDGE,"E136"),sQuery(id+"F0.wireOp",EDGE,"E137"),sQuery(id+"F0.wireOp",EDGE,"E138"),sQuery(id+"F0.wireOp",EDGE,"E139"),sQuery(id+"F0.wireOp",EDGE,"E140"),sQuery(id+"F0.wireOp",EDGE,"E141"),sQuery(id+"F0.wireOp",EDGE,"E142"),sQuery(id+"F0.wireOp",EDGE,"E143"),sQuery(id+"F0.wireOp",EDGE,"E144"),sQuery(id+"F0.wireOp",EDGE,"E145"),sQuery(id+"F0.wireOp",EDGE,"E146"),sQuery(id+"F0.wireOp",EDGE,"E147"),sQuery(id+"F0.wireOp",EDGE,"E148"),sQuery(id+"F0.wireOp",EDGE,"E149"),sQuery(id+"F0.wireOp",EDGE,"E150"),sQuery(id+"F0.wireOp",EDGE,"E151"),sQuery(id+"F0.wireOp",EDGE,"E152"),sQuery(id+"F0.wireOp",EDGE,"E153"),sQuery(id+"F0.wireOp",EDGE,"E154"),sQuery(id+"F0.wireOp",EDGE,"E155"),sQuery(id+"F0.wireOp",EDGE,"E156"),sQuery(id+"F0.wireOp",EDGE,"E157"),sQuery(id+"F0.wireOp",EDGE,"E158"),sQuery(id+"F0.wireOp",EDGE,"E159"),sQuery(id+"F0.wireOp",EDGE,"E160")])],"isStart":false}),makeQuery(id+"F4.hole-18.opRevolve","SWEPT_FACE",FACE,{"disambiguationData":[OSD([sQuery(id+"F4.hole-18.sketch.wireOp",EDGE,"core_line_2")])]})]})}),1.0]])]});
            extrude(context, id + "F6", {"entities" : qUnion([Q0, Q1, Q2, Q3, Q4]), "depth" : 20 * mm, "offsetDistance" : 25 * mm});
        }
        {
            var Q0;
            Q0=makeQuery(id+"F6.opExtrude","CAP_EDGE",EDGE,{"disambiguationData":[OSD([sQuery(id+"F5.wireOp",EDGE,"E187.right")])],"isStart":false});
            var Q1;
            Q1=makeQuery(id+"F6.opExtrude","CAP_EDGE",EDGE,{"disambiguationData":[OSD([sQuery(id+"F5.wireOp",EDGE,"E189.right")])],"isStart":false});
            fillet(context, id + "F7", {"entities" : qUnion([Q0, Q1]), "radius" : 5 * mm, "tangentPropagation" : true, "allowEdgeOverflow" : false});
        }
        {
            var Q0;
            Q0=sQuery(id+"F5.wireOp",VERTEX,"E185.center");
            var Q1;
            Q1=sQuery(id+"F5.wireOp",VERTEX,"E188");
            var Q2;
            Q2=sQuery(id+"F5.wireOp",VERTEX,"E190.0");
            var Q3;
            Q3=makeQuery(id+"F6.opExtrude","SWEPT_BODY",BODY,{"disambiguationData":[OSD([sQuery(id+"F5.wireOp",EDGE,"E187.bottom"),sQuery(id+"F5.wireOp",EDGE,"E187.top"),sQuery(id+"F5.wireOp",EDGE,"E187.left"),sQuery(id+"F5.wireOp",EDGE,"E187.right")])]});
            var Q4;
            Q4=makeQuery(id+"F6.opExtrude","SWEPT_BODY",BODY,{"disambiguationData":[OSD([sQuery(id+"F5.wireOp",EDGE,"E189.bottom"),sQuery(id+"F5.wireOp",EDGE,"E189.top"),sQuery(id+"F5.wireOp",EDGE,"E187.right"),sQuery(id+"F5.wireOp",EDGE,"E189.right")])]});
            hole(context, id + "F8", {"style" : HoleStyle.SIMPLE, "endStyle" : HoleEndStyle.BLIND, "oppositeDirection" : true, "standardTappedOrClearance" : lookupTablePath({ "standard" : "ISO", "fit" : "Normal", "size" : "M3", "type" : "Clearance" }), "standardBlindInLast" : lookupTablePath({ "fit" : "Standard", "standard" : "ISO", "size" : "M3", "type" : "Clearance" }), "holeDiameter" : 3.3 * mm, "holeDepth" : 15 * mm, "isTappedThrough" : true, "tappedDepth" : 12 * mm, "tapClearance" : 3, "startFromSketch" : true, "locations" : qUnion([Q0, Q1, Q2]), "scope" : qUnion([Q3, Q4])});
        }
        {
            var Q0;
            {var subQ167=sQuery(id+"F0.wireOp",EDGE,"E0");Q0=makeQuery(id+"F5.imprint","IMPRINT",FACE,{"disambiguationData":[TD([[makeQuery(id+"F5.imprint","IMPRINT",EDGE,{"derivedFrom":makeQuery(id+"F1.opExtrude","CAP_EDGE",EDGE,{"disambiguationData":[OSD([subQ167])],"isStart":false})}),1.0]])]});}
            var sketch = newSketch(context, id + "F9", { "sketchPlane" : qUnion([Q0])});
            skLineSegment(sketch, "E191.bottom", {"start": v(-0.25, 53.12) * mm, "end": v(24.75, 53.12) * mm});
            skLineSegment(sketch, "E191.top", {"start": v(-0.25, 46.12) * mm, "end": v(24.75, 46.12) * mm});
            skLineSegment(sketch, "E191.left", {"start": v(-0.25, 53.12) * mm, "end": v(-0.25, 46.12) * mm});
            skLineSegment(sketch, "E191.right", {"start": v(24.75, 53.12) * mm, "end": v(24.75, 46.12) * mm});
            skPoint(sketch, "E192.0", {"position": v(3.25, 49.62) * mm});
            skPoint(sketch, "E193.0", {"position": v(21.25, 49.62) * mm});
            skCircle(sketch, "E194", {"center": v(3.25, 49.62) * mm, "radius": 3.5 * mm, "construction": true});
            skPoint(sketch, "E195", {"position": v(-0.25, 49.62) * mm});
            skCircle(sketch, "E196", {"center": v(21.25, 49.62) * mm, "radius": 3.5 * mm, "construction": true});
            skCircle(sketch, "E197.0.0", {"center": v(-15.47, 44) * mm, "radius": 1.65 * mm});
            skPoint(sketch, "E198.0", {"position": v(12.25, 49.62) * mm});
            skSolve(sketch);
        }
        {
            var Q0;
            Q0=makeQuery(id+"F9.imprint","IMPRINT",FACE,{"disambiguationData":[TD([[makeQuery(id+"F9.imprint","IMPRINT",EDGE,{"derivedFrom":sQuery(id+"F9.wireOp",EDGE,"E191.bottom")}),-1.0]])]});
            var Q1;
            Q1=makeQuery(id+"F9.imprint","IMPRINT",FACE,{"disambiguationData":[TD([[makeQuery(id+"F9.imprint","IMPRINT",EDGE,{"derivedFrom":makeQuery(id+"F5.imprint","IMPRINT",EDGE,{"derivedFrom":makeQuery(id+"F4.hole-14.boolean.opBoolean","INTERSECT",EDGE,{"derivedFrom":[makeQuery(id+"F1.opExtrude","CAP_FACE",FACE,{"disambiguationData":[OSD([sQuery(id+"F0.wireOp",EDGE,"E0"),sQuery(id+"F0.wireOp",EDGE,"E1"),sQuery(id+"F0.wireOp",EDGE,"E2"),sQuery(id+"F0.wireOp",EDGE,"E4"),sQuery(id+"F0.wireOp",EDGE,"E5"),sQuery(id+"F0.wireOp",EDGE,"E6"),sQuery(id+"F0.wireOp",EDGE,"E7"),sQuery(id+"F0.wireOp",EDGE,"E8"),sQuery(id+"F0.wireOp",EDGE,"E9"),sQuery(id+"F0.wireOp",EDGE,"E10"),sQuery(id+"F0.wireOp",EDGE,"E11"),sQuery(id+"F0.wireOp",EDGE,"E12"),sQuery(id+"F0.wireOp",EDGE,"E13"),sQuery(id+"F0.wireOp",EDGE,"E14"),sQuery(id+"F0.wireOp",EDGE,"E15"),sQuery(id+"F0.wireOp",EDGE,"E16"),sQuery(id+"F0.wireOp",EDGE,"E17"),sQuery(id+"F0.wireOp",EDGE,"E18"),sQuery(id+"F0.wireOp",EDGE,"E19"),sQuery(id+"F0.wireOp",EDGE,"E20"),sQuery(id+"F0.wireOp",EDGE,"E21"),sQuery(id+"F0.wireOp",EDGE,"E22"),sQuery(id+"F0.wireOp",EDGE,"E23"),sQuery(id+"F0.wireOp",EDGE,"E24"),sQuery(id+"F0.wireOp",EDGE,"E25"),sQuery(id+"F0.wireOp",EDGE,"E26"),sQuery(id+"F0.wireOp",EDGE,"E27"),sQuery(id+"F0.wireOp",EDGE,"E28"),sQuery(id+"F0.wireOp",EDGE,"E29"),sQuery(id+"F0.wireOp",EDGE,"E30"),sQuery(id+"F0.wireOp",EDGE,"E31"),sQuery(id+"F0.wireOp",EDGE,"E32"),sQuery(id+"F0.wireOp",EDGE,"E33"),sQuery(id+"F0.wireOp",EDGE,"E34"),sQuery(id+"F0.wireOp",EDGE,"E35"),sQuery(id+"F0.wireOp",EDGE,"E36"),sQuery(id+"F0.wireOp",EDGE,"E37"),sQuery(id+"F0.wireOp",EDGE,"E38"),sQuery(id+"F0.wireOp",EDGE,"E39"),sQuery(id+"F0.wireOp",EDGE,"E40"),sQuery(id+"F0.wireOp",EDGE,"E42"),sQuery(id+"F0.wireOp",EDGE,"E43"),sQuery(id+"F0.wireOp",EDGE,"E45"),sQuery(id+"F0.wireOp",EDGE,"E46"),sQuery(id+"F0.wireOp",EDGE,"E47"),sQuery(id+"F0.wireOp",EDGE,"E48"),sQuery(id+"F0.wireOp",EDGE,"E49"),sQuery(id+"F0.wireOp",EDGE,"E50"),sQuery(id+"F0.wireOp",EDGE,"E44"),sQuery(id+"F0.wireOp",EDGE,"E51"),sQuery(id+"F0.wireOp",EDGE,"E52"),sQuery(id+"F0.wireOp",EDGE,"E53"),sQuery(id+"F0.wireOp",EDGE,"E54"),sQuery(id+"F0.wireOp",EDGE,"E55"),sQuery(id+"F0.wireOp",EDGE,"E56"),sQuery(id+"F0.wireOp",EDGE,"E57"),sQuery(id+"F0.wireOp",EDGE,"E58"),sQuery(id+"F0.wireOp",EDGE,"E59"),sQuery(id+"F0.wireOp",EDGE,"E60"),sQuery(id+"F0.wireOp",EDGE,"E61"),sQuery(id+"F0.wireOp",EDGE,"E62"),sQuery(id+"F0.wireOp",EDGE,"E63"),sQuery(id+"F0.wireOp",EDGE,"E64"),sQuery(id+"F0.wireOp",EDGE,"E65"),sQuery(id+"F0.wireOp",EDGE,"E66"),sQuery(id+"F0.wireOp",EDGE,"E67"),sQuery(id+"F0.wireOp",EDGE,"E68"),sQuery(id+"F0.wireOp",EDGE,"E69"),sQuery(id+"F0.wireOp",EDGE,"E70"),sQuery(id+"F0.wireOp",EDGE,"E71"),sQuery(id+"F0.wireOp",EDGE,"E72"),sQuery(id+"F0.wireOp",EDGE,"E73"),sQuery(id+"F0.wireOp",EDGE,"E74"),sQuery(id+"F0.wireOp",EDGE,"E75"),sQuery(id+"F0.wireOp",EDGE,"E76"),sQuery(id+"F0.wireOp",EDGE,"E77"),sQuery(id+"F0.wireOp",EDGE,"E78"),sQuery(id+"F0.wireOp",EDGE,"E79"),sQuery(id+"F0.wireOp",EDGE,"E80"),sQuery(id+"F0.wireOp",EDGE,"E81"),sQuery(id+"F0.wireOp",EDGE,"E82"),sQuery(id+"F0.wireOp",EDGE,"E83"),sQuery(id+"F0.wireOp",EDGE,"E84"),sQuery(id+"F0.wireOp",EDGE,"E85"),sQuery(id+"F0.wireOp",EDGE,"E86"),sQuery(id+"F0.wireOp",EDGE,"E87"),sQuery(id+"F0.wireOp",EDGE,"E88"),sQuery(id+"F0.wireOp",EDGE,"E89"),sQuery(id+"F0.wireOp",EDGE,"E90"),sQuery(id+"F0.wireOp",EDGE,"E91"),sQuery(id+"F0.wireOp",EDGE,"E92"),sQuery(id+"F0.wireOp",EDGE,"E93"),sQuery(id+"F0.wireOp",EDGE,"E94"),sQuery(id+"F0.wireOp",EDGE,"E95"),sQuery(id+"F0.wireOp",EDGE,"E96"),sQuery(id+"F0.wireOp",EDGE,"E97"),sQuery(id+"F0.wireOp",EDGE,"E98"),sQuery(id+"F0.wireOp",EDGE,"E99"),sQuery(id+"F0.wireOp",EDGE,"E100"),sQuery(id+"F0.wireOp",EDGE,"E101"),sQuery(id+"F0.wireOp",EDGE,"E102"),sQuery(id+"F0.wireOp",EDGE,"E103"),sQuery(id+"F0.wireOp",EDGE,"E104"),sQuery(id+"F0.wireOp",EDGE,"E105"),sQuery(id+"F0.wireOp",EDGE,"E106"),sQuery(id+"F0.wireOp",EDGE,"E107"),sQuery(id+"F0.wireOp",EDGE,"E108"),sQuery(id+"F0.wireOp",EDGE,"E109"),sQuery(id+"F0.wireOp",EDGE,"E110"),sQuery(id+"F0.wireOp",EDGE,"E111"),sQuery(id+"F0.wireOp",EDGE,"E112"),sQuery(id+"F0.wireOp",EDGE,"E113"),sQuery(id+"F0.wireOp",EDGE,"E114"),sQuery(id+"F0.wireOp",EDGE,"E115"),sQuery(id+"F0.wireOp",EDGE,"E116"),sQuery(id+"F0.wireOp",EDGE,"E117"),sQuery(id+"F0.wireOp",EDGE,"E118"),sQuery(id+"F0.wireOp",EDGE,"E119"),sQuery(id+"F0.wireOp",EDGE,"E120"),sQuery(id+"F0.wireOp",EDGE,"E121"),sQuery(id+"F0.wireOp",EDGE,"E122"),sQuery(id+"F0.wireOp",EDGE,"E123"),sQuery(id+"F0.wireOp",EDGE,"E124"),sQuery(id+"F0.wireOp",EDGE,"E125"),sQuery(id+"F0.wireOp",EDGE,"E126"),sQuery(id+"F0.wireOp",EDGE,"E127"),sQuery(id+"F0.wireOp",EDGE,"E128"),sQuery(id+"F0.wireOp",EDGE,"E129"),sQuery(id+"F0.wireOp",EDGE,"E130"),sQuery(id+"F0.wireOp",EDGE,"E131"),sQuery(id+"F0.wireOp",EDGE,"E132"),sQuery(id+"F0.wireOp",EDGE,"E133"),sQuery(id+"F0.wireOp",EDGE,"E134"),sQuery(id+"F0.wireOp",EDGE,"E135"),sQuery(id+"F0.wireOp",EDGE,"E136"),sQuery(id+"F0.wireOp",EDGE,"E137"),sQuery(id+"F0.wireOp",EDGE,"E138"),sQuery(id+"F0.wireOp",EDGE,"E139"),sQuery(id+"F0.wireOp",EDGE,"E140"),sQuery(id+"F0.wireOp",EDGE,"E141"),sQuery(id+"F0.wireOp",EDGE,"E142"),sQuery(id+"F0.wireOp",EDGE,"E143"),sQuery(id+"F0.wireOp",EDGE,"E144"),sQuery(id+"F0.wireOp",EDGE,"E145"),sQuery(id+"F0.wireOp",EDGE,"E146"),sQuery(id+"F0.wireOp",EDGE,"E147"),sQuery(id+"F0.wireOp",EDGE,"E148"),sQuery(id+"F0.wireOp",EDGE,"E149"),sQuery(id+"F0.wireOp",EDGE,"E150"),sQuery(id+"F0.wireOp",EDGE,"E151"),sQuery(id+"F0.wireOp",EDGE,"E152"),sQuery(id+"F0.wireOp",EDGE,"E153"),sQuery(id+"F0.wireOp",EDGE,"E154"),sQuery(id+"F0.wireOp",EDGE,"E155"),sQuery(id+"F0.wireOp",EDGE,"E156"),sQuery(id+"F0.wireOp",EDGE,"E157"),sQuery(id+"F0.wireOp",EDGE,"E158"),sQuery(id+"F0.wireOp",EDGE,"E159"),sQuery(id+"F0.wireOp",EDGE,"E160")])],"isStart":false}),makeQuery(id+"F4.hole-14.opRevolve","SWEPT_FACE",FACE,{"disambiguationData":[OSD([sQuery(id+"F4.hole-14.sketch.wireOp",EDGE,"core_line_2")])]})]})})}),1.0]])]});
            var Q2;
            Q2=makeQuery(id+"F9.imprint","IMPRINT",FACE,{"disambiguationData":[TD([[makeQuery(id+"F9.imprint","IMPRINT",EDGE,{"derivedFrom":makeQuery(id+"F5.imprint","IMPRINT",EDGE,{"derivedFrom":makeQuery(id+"F4.hole-15.boolean.opBoolean","INTERSECT",EDGE,{"derivedFrom":[makeQuery(id+"F1.opExtrude","CAP_FACE",FACE,{"disambiguationData":[OSD([sQuery(id+"F0.wireOp",EDGE,"E0"),sQuery(id+"F0.wireOp",EDGE,"E1"),sQuery(id+"F0.wireOp",EDGE,"E2"),sQuery(id+"F0.wireOp",EDGE,"E4"),sQuery(id+"F0.wireOp",EDGE,"E5"),sQuery(id+"F0.wireOp",EDGE,"E6"),sQuery(id+"F0.wireOp",EDGE,"E7"),sQuery(id+"F0.wireOp",EDGE,"E8"),sQuery(id+"F0.wireOp",EDGE,"E9"),sQuery(id+"F0.wireOp",EDGE,"E10"),sQuery(id+"F0.wireOp",EDGE,"E11"),sQuery(id+"F0.wireOp",EDGE,"E12"),sQuery(id+"F0.wireOp",EDGE,"E13"),sQuery(id+"F0.wireOp",EDGE,"E14"),sQuery(id+"F0.wireOp",EDGE,"E15"),sQuery(id+"F0.wireOp",EDGE,"E16"),sQuery(id+"F0.wireOp",EDGE,"E17"),sQuery(id+"F0.wireOp",EDGE,"E18"),sQuery(id+"F0.wireOp",EDGE,"E19"),sQuery(id+"F0.wireOp",EDGE,"E20"),sQuery(id+"F0.wireOp",EDGE,"E21"),sQuery(id+"F0.wireOp",EDGE,"E22"),sQuery(id+"F0.wireOp",EDGE,"E23"),sQuery(id+"F0.wireOp",EDGE,"E24"),sQuery(id+"F0.wireOp",EDGE,"E25"),sQuery(id+"F0.wireOp",EDGE,"E26"),sQuery(id+"F0.wireOp",EDGE,"E27"),sQuery(id+"F0.wireOp",EDGE,"E28"),sQuery(id+"F0.wireOp",EDGE,"E29"),sQuery(id+"F0.wireOp",EDGE,"E30"),sQuery(id+"F0.wireOp",EDGE,"E31"),sQuery(id+"F0.wireOp",EDGE,"E32"),sQuery(id+"F0.wireOp",EDGE,"E33"),sQuery(id+"F0.wireOp",EDGE,"E34"),sQuery(id+"F0.wireOp",EDGE,"E35"),sQuery(id+"F0.wireOp",EDGE,"E36"),sQuery(id+"F0.wireOp",EDGE,"E37"),sQuery(id+"F0.wireOp",EDGE,"E38"),sQuery(id+"F0.wireOp",EDGE,"E39"),sQuery(id+"F0.wireOp",EDGE,"E40"),sQuery(id+"F0.wireOp",EDGE,"E42"),sQuery(id+"F0.wireOp",EDGE,"E43"),sQuery(id+"F0.wireOp",EDGE,"E45"),sQuery(id+"F0.wireOp",EDGE,"E46"),sQuery(id+"F0.wireOp",EDGE,"E47"),sQuery(id+"F0.wireOp",EDGE,"E48"),sQuery(id+"F0.wireOp",EDGE,"E49"),sQuery(id+"F0.wireOp",EDGE,"E50"),sQuery(id+"F0.wireOp",EDGE,"E44"),sQuery(id+"F0.wireOp",EDGE,"E51"),sQuery(id+"F0.wireOp",EDGE,"E52"),sQuery(id+"F0.wireOp",EDGE,"E53"),sQuery(id+"F0.wireOp",EDGE,"E54"),sQuery(id+"F0.wireOp",EDGE,"E55"),sQuery(id+"F0.wireOp",EDGE,"E56"),sQuery(id+"F0.wireOp",EDGE,"E57"),sQuery(id+"F0.wireOp",EDGE,"E58"),sQuery(id+"F0.wireOp",EDGE,"E59"),sQuery(id+"F0.wireOp",EDGE,"E60"),sQuery(id+"F0.wireOp",EDGE,"E61"),sQuery(id+"F0.wireOp",EDGE,"E62"),sQuery(id+"F0.wireOp",EDGE,"E63"),sQuery(id+"F0.wireOp",EDGE,"E64"),sQuery(id+"F0.wireOp",EDGE,"E65"),sQuery(id+"F0.wireOp",EDGE,"E66"),sQuery(id+"F0.wireOp",EDGE,"E67"),sQuery(id+"F0.wireOp",EDGE,"E68"),sQuery(id+"F0.wireOp",EDGE,"E69"),sQuery(id+"F0.wireOp",EDGE,"E70"),sQuery(id+"F0.wireOp",EDGE,"E71"),sQuery(id+"F0.wireOp",EDGE,"E72"),sQuery(id+"F0.wireOp",EDGE,"E73"),sQuery(id+"F0.wireOp",EDGE,"E74"),sQuery(id+"F0.wireOp",EDGE,"E75"),sQuery(id+"F0.wireOp",EDGE,"E76"),sQuery(id+"F0.wireOp",EDGE,"E77"),sQuery(id+"F0.wireOp",EDGE,"E78"),sQuery(id+"F0.wireOp",EDGE,"E79"),sQuery(id+"F0.wireOp",EDGE,"E80"),sQuery(id+"F0.wireOp",EDGE,"E81"),sQuery(id+"F0.wireOp",EDGE,"E82"),sQuery(id+"F0.wireOp",EDGE,"E83"),sQuery(id+"F0.wireOp",EDGE,"E84"),sQuery(id+"F0.wireOp",EDGE,"E85"),sQuery(id+"F0.wireOp",EDGE,"E86"),sQuery(id+"F0.wireOp",EDGE,"E87"),sQuery(id+"F0.wireOp",EDGE,"E88"),sQuery(id+"F0.wireOp",EDGE,"E89"),sQuery(id+"F0.wireOp",EDGE,"E90"),sQuery(id+"F0.wireOp",EDGE,"E91"),sQuery(id+"F0.wireOp",EDGE,"E92"),sQuery(id+"F0.wireOp",EDGE,"E93"),sQuery(id+"F0.wireOp",EDGE,"E94"),sQuery(id+"F0.wireOp",EDGE,"E95"),sQuery(id+"F0.wireOp",EDGE,"E96"),sQuery(id+"F0.wireOp",EDGE,"E97"),sQuery(id+"F0.wireOp",EDGE,"E98"),sQuery(id+"F0.wireOp",EDGE,"E99"),sQuery(id+"F0.wireOp",EDGE,"E100"),sQuery(id+"F0.wireOp",EDGE,"E101"),sQuery(id+"F0.wireOp",EDGE,"E102"),sQuery(id+"F0.wireOp",EDGE,"E103"),sQuery(id+"F0.wireOp",EDGE,"E104"),sQuery(id+"F0.wireOp",EDGE,"E105"),sQuery(id+"F0.wireOp",EDGE,"E106"),sQuery(id+"F0.wireOp",EDGE,"E107"),sQuery(id+"F0.wireOp",EDGE,"E108"),sQuery(id+"F0.wireOp",EDGE,"E109"),sQuery(id+"F0.wireOp",EDGE,"E110"),sQuery(id+"F0.wireOp",EDGE,"E111"),sQuery(id+"F0.wireOp",EDGE,"E112"),sQuery(id+"F0.wireOp",EDGE,"E113"),sQuery(id+"F0.wireOp",EDGE,"E114"),sQuery(id+"F0.wireOp",EDGE,"E115"),sQuery(id+"F0.wireOp",EDGE,"E116"),sQuery(id+"F0.wireOp",EDGE,"E117"),sQuery(id+"F0.wireOp",EDGE,"E118"),sQuery(id+"F0.wireOp",EDGE,"E119"),sQuery(id+"F0.wireOp",EDGE,"E120"),sQuery(id+"F0.wireOp",EDGE,"E121"),sQuery(id+"F0.wireOp",EDGE,"E122"),sQuery(id+"F0.wireOp",EDGE,"E123"),sQuery(id+"F0.wireOp",EDGE,"E124"),sQuery(id+"F0.wireOp",EDGE,"E125"),sQuery(id+"F0.wireOp",EDGE,"E126"),sQuery(id+"F0.wireOp",EDGE,"E127"),sQuery(id+"F0.wireOp",EDGE,"E128"),sQuery(id+"F0.wireOp",EDGE,"E129"),sQuery(id+"F0.wireOp",EDGE,"E130"),sQuery(id+"F0.wireOp",EDGE,"E131"),sQuery(id+"F0.wireOp",EDGE,"E132"),sQuery(id+"F0.wireOp",EDGE,"E133"),sQuery(id+"F0.wireOp",EDGE,"E134"),sQuery(id+"F0.wireOp",EDGE,"E135"),sQuery(id+"F0.wireOp",EDGE,"E136"),sQuery(id+"F0.wireOp",EDGE,"E137"),sQuery(id+"F0.wireOp",EDGE,"E138"),sQuery(id+"F0.wireOp",EDGE,"E139"),sQuery(id+"F0.wireOp",EDGE,"E140"),sQuery(id+"F0.wireOp",EDGE,"E141"),sQuery(id+"F0.wireOp",EDGE,"E142"),sQuery(id+"F0.wireOp",EDGE,"E143"),sQuery(id+"F0.wireOp",EDGE,"E144"),sQuery(id+"F0.wireOp",EDGE,"E145"),sQuery(id+"F0.wireOp",EDGE,"E146"),sQuery(id+"F0.wireOp",EDGE,"E147"),sQuery(id+"F0.wireOp",EDGE,"E148"),sQuery(id+"F0.wireOp",EDGE,"E149"),sQuery(id+"F0.wireOp",EDGE,"E150"),sQuery(id+"F0.wireOp",EDGE,"E151"),sQuery(id+"F0.wireOp",EDGE,"E152"),sQuery(id+"F0.wireOp",EDGE,"E153"),sQuery(id+"F0.wireOp",EDGE,"E154"),sQuery(id+"F0.wireOp",EDGE,"E155"),sQuery(id+"F0.wireOp",EDGE,"E156"),sQuery(id+"F0.wireOp",EDGE,"E157"),sQuery(id+"F0.wireOp",EDGE,"E158"),sQuery(id+"F0.wireOp",EDGE,"E159"),sQuery(id+"F0.wireOp",EDGE,"E160")])],"isStart":false}),makeQuery(id+"F4.hole-15.opRevolve","SWEPT_FACE",FACE,{"disambiguationData":[OSD([sQuery(id+"F4.hole-15.sketch.wireOp",EDGE,"core_line_2")])]})]})})}),1.0]])]});
            var Q3;
            Q3=makeQuery(id+"F9.imprint","IMPRINT",FACE,{"disambiguationData":[TD([[makeQuery(id+"F9.imprint","IMPRINT",EDGE,{"derivedFrom":makeQuery(id+"F5.imprint","IMPRINT",EDGE,{"derivedFrom":makeQuery(id+"F4.hole-16.boolean.opBoolean","INTERSECT",EDGE,{"derivedFrom":[makeQuery(id+"F1.opExtrude","CAP_FACE",FACE,{"disambiguationData":[OSD([sQuery(id+"F0.wireOp",EDGE,"E0"),sQuery(id+"F0.wireOp",EDGE,"E1"),sQuery(id+"F0.wireOp",EDGE,"E2"),sQuery(id+"F0.wireOp",EDGE,"E4"),sQuery(id+"F0.wireOp",EDGE,"E5"),sQuery(id+"F0.wireOp",EDGE,"E6"),sQuery(id+"F0.wireOp",EDGE,"E7"),sQuery(id+"F0.wireOp",EDGE,"E8"),sQuery(id+"F0.wireOp",EDGE,"E9"),sQuery(id+"F0.wireOp",EDGE,"E10"),sQuery(id+"F0.wireOp",EDGE,"E11"),sQuery(id+"F0.wireOp",EDGE,"E12"),sQuery(id+"F0.wireOp",EDGE,"E13"),sQuery(id+"F0.wireOp",EDGE,"E14"),sQuery(id+"F0.wireOp",EDGE,"E15"),sQuery(id+"F0.wireOp",EDGE,"E16"),sQuery(id+"F0.wireOp",EDGE,"E17"),sQuery(id+"F0.wireOp",EDGE,"E18"),sQuery(id+"F0.wireOp",EDGE,"E19"),sQuery(id+"F0.wireOp",EDGE,"E20"),sQuery(id+"F0.wireOp",EDGE,"E21"),sQuery(id+"F0.wireOp",EDGE,"E22"),sQuery(id+"F0.wireOp",EDGE,"E23"),sQuery(id+"F0.wireOp",EDGE,"E24"),sQuery(id+"F0.wireOp",EDGE,"E25"),sQuery(id+"F0.wireOp",EDGE,"E26"),sQuery(id+"F0.wireOp",EDGE,"E27"),sQuery(id+"F0.wireOp",EDGE,"E28"),sQuery(id+"F0.wireOp",EDGE,"E29"),sQuery(id+"F0.wireOp",EDGE,"E30"),sQuery(id+"F0.wireOp",EDGE,"E31"),sQuery(id+"F0.wireOp",EDGE,"E32"),sQuery(id+"F0.wireOp",EDGE,"E33"),sQuery(id+"F0.wireOp",EDGE,"E34"),sQuery(id+"F0.wireOp",EDGE,"E35"),sQuery(id+"F0.wireOp",EDGE,"E36"),sQuery(id+"F0.wireOp",EDGE,"E37"),sQuery(id+"F0.wireOp",EDGE,"E38"),sQuery(id+"F0.wireOp",EDGE,"E39"),sQuery(id+"F0.wireOp",EDGE,"E40"),sQuery(id+"F0.wireOp",EDGE,"E42"),sQuery(id+"F0.wireOp",EDGE,"E43"),sQuery(id+"F0.wireOp",EDGE,"E45"),sQuery(id+"F0.wireOp",EDGE,"E46"),sQuery(id+"F0.wireOp",EDGE,"E47"),sQuery(id+"F0.wireOp",EDGE,"E48"),sQuery(id+"F0.wireOp",EDGE,"E49"),sQuery(id+"F0.wireOp",EDGE,"E50"),sQuery(id+"F0.wireOp",EDGE,"E44"),sQuery(id+"F0.wireOp",EDGE,"E51"),sQuery(id+"F0.wireOp",EDGE,"E52"),sQuery(id+"F0.wireOp",EDGE,"E53"),sQuery(id+"F0.wireOp",EDGE,"E54"),sQuery(id+"F0.wireOp",EDGE,"E55"),sQuery(id+"F0.wireOp",EDGE,"E56"),sQuery(id+"F0.wireOp",EDGE,"E57"),sQuery(id+"F0.wireOp",EDGE,"E58"),sQuery(id+"F0.wireOp",EDGE,"E59"),sQuery(id+"F0.wireOp",EDGE,"E60"),sQuery(id+"F0.wireOp",EDGE,"E61"),sQuery(id+"F0.wireOp",EDGE,"E62"),sQuery(id+"F0.wireOp",EDGE,"E63"),sQuery(id+"F0.wireOp",EDGE,"E64"),sQuery(id+"F0.wireOp",EDGE,"E65"),sQuery(id+"F0.wireOp",EDGE,"E66"),sQuery(id+"F0.wireOp",EDGE,"E67"),sQuery(id+"F0.wireOp",EDGE,"E68"),sQuery(id+"F0.wireOp",EDGE,"E69"),sQuery(id+"F0.wireOp",EDGE,"E70"),sQuery(id+"F0.wireOp",EDGE,"E71"),sQuery(id+"F0.wireOp",EDGE,"E72"),sQuery(id+"F0.wireOp",EDGE,"E73"),sQuery(id+"F0.wireOp",EDGE,"E74"),sQuery(id+"F0.wireOp",EDGE,"E75"),sQuery(id+"F0.wireOp",EDGE,"E76"),sQuery(id+"F0.wireOp",EDGE,"E77"),sQuery(id+"F0.wireOp",EDGE,"E78"),sQuery(id+"F0.wireOp",EDGE,"E79"),sQuery(id+"F0.wireOp",EDGE,"E80"),sQuery(id+"F0.wireOp",EDGE,"E81"),sQuery(id+"F0.wireOp",EDGE,"E82"),sQuery(id+"F0.wireOp",EDGE,"E83"),sQuery(id+"F0.wireOp",EDGE,"E84"),sQuery(id+"F0.wireOp",EDGE,"E85"),sQuery(id+"F0.wireOp",EDGE,"E86"),sQuery(id+"F0.wireOp",EDGE,"E87"),sQuery(id+"F0.wireOp",EDGE,"E88"),sQuery(id+"F0.wireOp",EDGE,"E89"),sQuery(id+"F0.wireOp",EDGE,"E90"),sQuery(id+"F0.wireOp",EDGE,"E91"),sQuery(id+"F0.wireOp",EDGE,"E92"),sQuery(id+"F0.wireOp",EDGE,"E93"),sQuery(id+"F0.wireOp",EDGE,"E94"),sQuery(id+"F0.wireOp",EDGE,"E95"),sQuery(id+"F0.wireOp",EDGE,"E96"),sQuery(id+"F0.wireOp",EDGE,"E97"),sQuery(id+"F0.wireOp",EDGE,"E98"),sQuery(id+"F0.wireOp",EDGE,"E99"),sQuery(id+"F0.wireOp",EDGE,"E100"),sQuery(id+"F0.wireOp",EDGE,"E101"),sQuery(id+"F0.wireOp",EDGE,"E102"),sQuery(id+"F0.wireOp",EDGE,"E103"),sQuery(id+"F0.wireOp",EDGE,"E104"),sQuery(id+"F0.wireOp",EDGE,"E105"),sQuery(id+"F0.wireOp",EDGE,"E106"),sQuery(id+"F0.wireOp",EDGE,"E107"),sQuery(id+"F0.wireOp",EDGE,"E108"),sQuery(id+"F0.wireOp",EDGE,"E109"),sQuery(id+"F0.wireOp",EDGE,"E110"),sQuery(id+"F0.wireOp",EDGE,"E111"),sQuery(id+"F0.wireOp",EDGE,"E112"),sQuery(id+"F0.wireOp",EDGE,"E113"),sQuery(id+"F0.wireOp",EDGE,"E114"),sQuery(id+"F0.wireOp",EDGE,"E115"),sQuery(id+"F0.wireOp",EDGE,"E116"),sQuery(id+"F0.wireOp",EDGE,"E117"),sQuery(id+"F0.wireOp",EDGE,"E118"),sQuery(id+"F0.wireOp",EDGE,"E119"),sQuery(id+"F0.wireOp",EDGE,"E120"),sQuery(id+"F0.wireOp",EDGE,"E121"),sQuery(id+"F0.wireOp",EDGE,"E122"),sQuery(id+"F0.wireOp",EDGE,"E123"),sQuery(id+"F0.wireOp",EDGE,"E124"),sQuery(id+"F0.wireOp",EDGE,"E125"),sQuery(id+"F0.wireOp",EDGE,"E126"),sQuery(id+"F0.wireOp",EDGE,"E127"),sQuery(id+"F0.wireOp",EDGE,"E128"),sQuery(id+"F0.wireOp",EDGE,"E129"),sQuery(id+"F0.wireOp",EDGE,"E130"),sQuery(id+"F0.wireOp",EDGE,"E131"),sQuery(id+"F0.wireOp",EDGE,"E132"),sQuery(id+"F0.wireOp",EDGE,"E133"),sQuery(id+"F0.wireOp",EDGE,"E134"),sQuery(id+"F0.wireOp",EDGE,"E135"),sQuery(id+"F0.wireOp",EDGE,"E136"),sQuery(id+"F0.wireOp",EDGE,"E137"),sQuery(id+"F0.wireOp",EDGE,"E138"),sQuery(id+"F0.wireOp",EDGE,"E139"),sQuery(id+"F0.wireOp",EDGE,"E140"),sQuery(id+"F0.wireOp",EDGE,"E141"),sQuery(id+"F0.wireOp",EDGE,"E142"),sQuery(id+"F0.wireOp",EDGE,"E143"),sQuery(id+"F0.wireOp",EDGE,"E144"),sQuery(id+"F0.wireOp",EDGE,"E145"),sQuery(id+"F0.wireOp",EDGE,"E146"),sQuery(id+"F0.wireOp",EDGE,"E147"),sQuery(id+"F0.wireOp",EDGE,"E148"),sQuery(id+"F0.wireOp",EDGE,"E149"),sQuery(id+"F0.wireOp",EDGE,"E150"),sQuery(id+"F0.wireOp",EDGE,"E151"),sQuery(id+"F0.wireOp",EDGE,"E152"),sQuery(id+"F0.wireOp",EDGE,"E153"),sQuery(id+"F0.wireOp",EDGE,"E154"),sQuery(id+"F0.wireOp",EDGE,"E155"),sQuery(id+"F0.wireOp",EDGE,"E156"),sQuery(id+"F0.wireOp",EDGE,"E157"),sQuery(id+"F0.wireOp",EDGE,"E158"),sQuery(id+"F0.wireOp",EDGE,"E159"),sQuery(id+"F0.wireOp",EDGE,"E160")])],"isStart":false}),makeQuery(id+"F4.hole-16.opRevolve","SWEPT_FACE",FACE,{"disambiguationData":[OSD([sQuery(id+"F4.hole-16.sketch.wireOp",EDGE,"core_line_2")])]})]})})}),1.0]])]});
            extrude(context, id + "F10", {"entities" : qUnion([Q0, Q1, Q2, Q3]), "depth" : 20 * mm, "offsetDistance" : 25 * mm});
        }
        {
            var Q0;
            Q0=sQuery(id+"F9.wireOp",VERTEX,"E192.0");
            var Q1;
            Q1=sQuery(id+"F9.wireOp",VERTEX,"E198.0");
            var Q2;
            Q2=sQuery(id+"F9.wireOp",VERTEX,"E193.0");
            var Q3;
            Q3=makeQuery(id+"F10.opExtrude","SWEPT_BODY",BODY,{"disambiguationData":[OSD([sQuery(id+"F0.wireOp",EDGE,"E0"),sQuery(id+"F0.wireOp",EDGE,"E1"),sQuery(id+"F0.wireOp",EDGE,"E2"),sQuery(id+"F0.wireOp",EDGE,"E4"),sQuery(id+"F0.wireOp",EDGE,"E5"),sQuery(id+"F0.wireOp",EDGE,"E6"),sQuery(id+"F0.wireOp",EDGE,"E7"),sQuery(id+"F0.wireOp",EDGE,"E8"),sQuery(id+"F0.wireOp",EDGE,"E9"),sQuery(id+"F0.wireOp",EDGE,"E10"),sQuery(id+"F0.wireOp",EDGE,"E11"),sQuery(id+"F0.wireOp",EDGE,"E12"),sQuery(id+"F0.wireOp",EDGE,"E13"),sQuery(id+"F0.wireOp",EDGE,"E14"),sQuery(id+"F0.wireOp",EDGE,"E15"),sQuery(id+"F0.wireOp",EDGE,"E16"),sQuery(id+"F0.wireOp",EDGE,"E17"),sQuery(id+"F0.wireOp",EDGE,"E18"),sQuery(id+"F0.wireOp",EDGE,"E19"),sQuery(id+"F0.wireOp",EDGE,"E20"),sQuery(id+"F0.wireOp",EDGE,"E21"),sQuery(id+"F0.wireOp",EDGE,"E22"),sQuery(id+"F0.wireOp",EDGE,"E23"),sQuery(id+"F0.wireOp",EDGE,"E24"),sQuery(id+"F0.wireOp",EDGE,"E25"),sQuery(id+"F0.wireOp",EDGE,"E26"),sQuery(id+"F0.wireOp",EDGE,"E27"),sQuery(id+"F0.wireOp",EDGE,"E28"),sQuery(id+"F0.wireOp",EDGE,"E29"),sQuery(id+"F0.wireOp",EDGE,"E30"),sQuery(id+"F0.wireOp",EDGE,"E31"),sQuery(id+"F0.wireOp",EDGE,"E32"),sQuery(id+"F0.wireOp",EDGE,"E33"),sQuery(id+"F0.wireOp",EDGE,"E34"),sQuery(id+"F0.wireOp",EDGE,"E35"),sQuery(id+"F0.wireOp",EDGE,"E36"),sQuery(id+"F0.wireOp",EDGE,"E37"),sQuery(id+"F0.wireOp",EDGE,"E38"),sQuery(id+"F0.wireOp",EDGE,"E39"),sQuery(id+"F0.wireOp",EDGE,"E40"),sQuery(id+"F0.wireOp",EDGE,"E42"),sQuery(id+"F0.wireOp",EDGE,"E43"),sQuery(id+"F0.wireOp",EDGE,"E45"),sQuery(id+"F0.wireOp",EDGE,"E46"),sQuery(id+"F0.wireOp",EDGE,"E47"),sQuery(id+"F0.wireOp",EDGE,"E48"),sQuery(id+"F0.wireOp",EDGE,"E49"),sQuery(id+"F0.wireOp",EDGE,"E50"),sQuery(id+"F0.wireOp",EDGE,"E44"),sQuery(id+"F0.wireOp",EDGE,"E51"),sQuery(id+"F0.wireOp",EDGE,"E52"),sQuery(id+"F0.wireOp",EDGE,"E53"),sQuery(id+"F0.wireOp",EDGE,"E54"),sQuery(id+"F0.wireOp",EDGE,"E55"),sQuery(id+"F0.wireOp",EDGE,"E56"),sQuery(id+"F0.wireOp",EDGE,"E57"),sQuery(id+"F0.wireOp",EDGE,"E58"),sQuery(id+"F0.wireOp",EDGE,"E59"),sQuery(id+"F0.wireOp",EDGE,"E60"),sQuery(id+"F0.wireOp",EDGE,"E61"),sQuery(id+"F0.wireOp",EDGE,"E62"),sQuery(id+"F0.wireOp",EDGE,"E63"),sQuery(id+"F0.wireOp",EDGE,"E64"),sQuery(id+"F0.wireOp",EDGE,"E65"),sQuery(id+"F0.wireOp",EDGE,"E66"),sQuery(id+"F0.wireOp",EDGE,"E67"),sQuery(id+"F0.wireOp",EDGE,"E68"),sQuery(id+"F0.wireOp",EDGE,"E69"),sQuery(id+"F0.wireOp",EDGE,"E70"),sQuery(id+"F0.wireOp",EDGE,"E71"),sQuery(id+"F0.wireOp",EDGE,"E72"),sQuery(id+"F0.wireOp",EDGE,"E73"),sQuery(id+"F0.wireOp",EDGE,"E74"),sQuery(id+"F0.wireOp",EDGE,"E75"),sQuery(id+"F0.wireOp",EDGE,"E76"),sQuery(id+"F0.wireOp",EDGE,"E77"),sQuery(id+"F0.wireOp",EDGE,"E78"),sQuery(id+"F0.wireOp",EDGE,"E79"),sQuery(id+"F0.wireOp",EDGE,"E80"),sQuery(id+"F0.wireOp",EDGE,"E81"),sQuery(id+"F0.wireOp",EDGE,"E82"),sQuery(id+"F0.wireOp",EDGE,"E83"),sQuery(id+"F0.wireOp",EDGE,"E84"),sQuery(id+"F0.wireOp",EDGE,"E85"),sQuery(id+"F0.wireOp",EDGE,"E86"),sQuery(id+"F0.wireOp",EDGE,"E87"),sQuery(id+"F0.wireOp",EDGE,"E88"),sQuery(id+"F0.wireOp",EDGE,"E89"),sQuery(id+"F0.wireOp",EDGE,"E90"),sQuery(id+"F0.wireOp",EDGE,"E91"),sQuery(id+"F0.wireOp",EDGE,"E92"),sQuery(id+"F0.wireOp",EDGE,"E93"),sQuery(id+"F0.wireOp",EDGE,"E94"),sQuery(id+"F0.wireOp",EDGE,"E95"),sQuery(id+"F0.wireOp",EDGE,"E96"),sQuery(id+"F0.wireOp",EDGE,"E97"),sQuery(id+"F0.wireOp",EDGE,"E98"),sQuery(id+"F0.wireOp",EDGE,"E99"),sQuery(id+"F0.wireOp",EDGE,"E100"),sQuery(id+"F0.wireOp",EDGE,"E101"),sQuery(id+"F0.wireOp",EDGE,"E102"),sQuery(id+"F0.wireOp",EDGE,"E103"),sQuery(id+"F0.wireOp",EDGE,"E104"),sQuery(id+"F0.wireOp",EDGE,"E105"),sQuery(id+"F0.wireOp",EDGE,"E106"),sQuery(id+"F0.wireOp",EDGE,"E107"),sQuery(id+"F0.wireOp",EDGE,"E108"),sQuery(id+"F0.wireOp",EDGE,"E109"),sQuery(id+"F0.wireOp",EDGE,"E110"),sQuery(id+"F0.wireOp",EDGE,"E111"),sQuery(id+"F0.wireOp",EDGE,"E112"),sQuery(id+"F0.wireOp",EDGE,"E113"),sQuery(id+"F0.wireOp",EDGE,"E114"),sQuery(id+"F0.wireOp",EDGE,"E115"),sQuery(id+"F0.wireOp",EDGE,"E116"),sQuery(id+"F0.wireOp",EDGE,"E117"),sQuery(id+"F0.wireOp",EDGE,"E118"),sQuery(id+"F0.wireOp",EDGE,"E119"),sQuery(id+"F0.wireOp",EDGE,"E120"),sQuery(id+"F0.wireOp",EDGE,"E121"),sQuery(id+"F0.wireOp",EDGE,"E122"),sQuery(id+"F0.wireOp",EDGE,"E123"),sQuery(id+"F0.wireOp",EDGE,"E124"),sQuery(id+"F0.wireOp",EDGE,"E125"),sQuery(id+"F0.wireOp",EDGE,"E126"),sQuery(id+"F0.wireOp",EDGE,"E127"),sQuery(id+"F0.wireOp",EDGE,"E128"),sQuery(id+"F0.wireOp",EDGE,"E129"),sQuery(id+"F0.wireOp",EDGE,"E130"),sQuery(id+"F0.wireOp",EDGE,"E131"),sQuery(id+"F0.wireOp",EDGE,"E132"),sQuery(id+"F0.wireOp",EDGE,"E133"),sQuery(id+"F0.wireOp",EDGE,"E134"),sQuery(id+"F0.wireOp",EDGE,"E135"),sQuery(id+"F0.wireOp",EDGE,"E136"),sQuery(id+"F0.wireOp",EDGE,"E137"),sQuery(id+"F0.wireOp",EDGE,"E138"),sQuery(id+"F0.wireOp",EDGE,"E139"),sQuery(id+"F0.wireOp",EDGE,"E140"),sQuery(id+"F0.wireOp",EDGE,"E141"),sQuery(id+"F0.wireOp",EDGE,"E142"),sQuery(id+"F0.wireOp",EDGE,"E143"),sQuery(id+"F0.wireOp",EDGE,"E144"),sQuery(id+"F0.wireOp",EDGE,"E145"),sQuery(id+"F0.wireOp",EDGE,"E146"),sQuery(id+"F0.wireOp",EDGE,"E147"),sQuery(id+"F0.wireOp",EDGE,"E148"),sQuery(id+"F0.wireOp",EDGE,"E149"),sQuery(id+"F0.wireOp",EDGE,"E150"),sQuery(id+"F0.wireOp",EDGE,"E151"),sQuery(id+"F0.wireOp",EDGE,"E152"),sQuery(id+"F0.wireOp",EDGE,"E153"),sQuery(id+"F0.wireOp",EDGE,"E154"),sQuery(id+"F0.wireOp",EDGE,"E155"),sQuery(id+"F0.wireOp",EDGE,"E156"),sQuery(id+"F0.wireOp",EDGE,"E157"),sQuery(id+"F0.wireOp",EDGE,"E158"),sQuery(id+"F0.wireOp",EDGE,"E159"),sQuery(id+"F0.wireOp",EDGE,"E160"),sQuery(id+"F4.hole-18.sketch.wireOp",EDGE,"core_line_2")])]});
            var Q4;
            Q4=makeQuery(id+"F10.opExtrude","SWEPT_BODY",BODY,{"disambiguationData":[OSD([sQuery(id+"F9.wireOp",EDGE,"E191.bottom"),sQuery(id+"F9.wireOp",EDGE,"E191.top"),sQuery(id+"F9.wireOp",EDGE,"E191.left"),sQuery(id+"F9.wireOp",EDGE,"E191.right")])]});
            hole(context, id + "F11", {"style" : HoleStyle.SIMPLE, "endStyle" : HoleEndStyle.BLIND, "oppositeDirection" : true, "standardTappedOrClearance" : lookupTablePath({ "standard" : "ISO", "fit" : "Normal", "size" : "M3", "type" : "Clearance" }), "standardBlindInLast" : lookupTablePath({ "fit" : "Standard", "standard" : "ISO", "size" : "M3", "type" : "Clearance" }), "holeDiameter" : 3.3 * mm, "holeDepth" : 15 * mm, "isTappedThrough" : true, "tappedDepth" : 12 * mm, "tapClearance" : 3, "startFromSketch" : true, "locations" : qUnion([Q0, Q1, Q2]), "scope" : qUnion([Q3, Q4])});
        }
        {
            var Q0;
            Q0=makeQuery(id+"F10.opExtrude","CAP_EDGE",EDGE,{"disambiguationData":[OSD([sQuery(id+"F9.wireOp",EDGE,"E191.left")])],"isStart":false});
            var Q1;
            Q1=makeQuery(id+"F10.opExtrude","CAP_EDGE",EDGE,{"disambiguationData":[OSD([sQuery(id+"F9.wireOp",EDGE,"E191.right")])],"isStart":false});
            fillet(context, id + "F12", {"entities" : qUnion([Q0, Q1]), "radius" : 5 * mm, "tangentPropagation" : true, "allowEdgeOverflow" : false});
        }
    });
